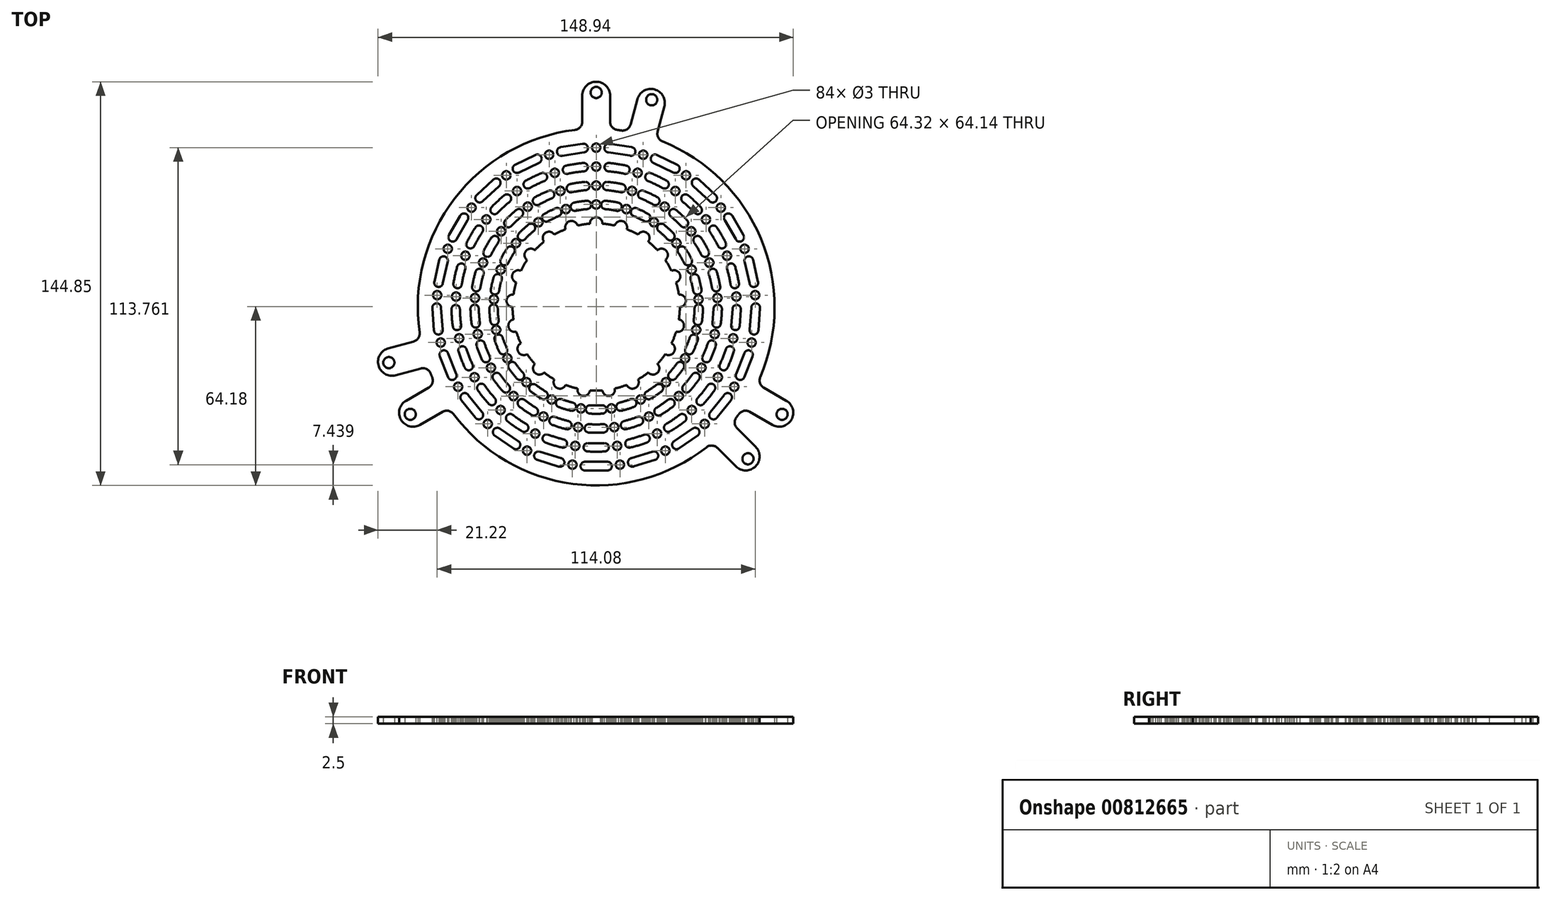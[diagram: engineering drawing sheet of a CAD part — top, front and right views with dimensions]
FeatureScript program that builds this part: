
annotation { "Feature Type Name" : "Feature", "Feature Type Description" : "" }
export const myFeature = defineFeature(function(context is Context, id is Id, definition is map)
    precondition{}
    {
        {
            var Q0;
            Q0=qCreatedBy(makeId("Top.planeOp"),FACE);
            var sketch = newSketch(context, id + "F0", { "sketchPlane" : qUnion([Q0])});
            skCircle(sketch, "E0", {"center": v(0, 0) * mm, "radius": 30 * mm});
            skCircle(sketch, "E1", {"center": v(0, 0) * mm, "radius": 64 * mm});
            skCircle(sketch, "E2", {"center": v(0, 0) * mm, "radius": 77 * mm, "construction": true});
            skCircle(sketch, "E3", {"center": v(0, 0) * mm, "radius": 81 * mm, "construction": true});
            skLineSegment(sketch, "E4", {"start": v(0, 0) * mm, "end": v(0, 81) * mm, "construction": true});
            skLineSegment(sketch, "E5", {"start": v(20.96, 78.24) * mm, "end": v(0, 0) * mm, "construction": true});
            skLineSegment(sketch, "E6", {"start": v(-5, 63.8) * mm, "end": v(-5, 80.85) * mm});
            skLineSegment(sketch, "E7", {"start": v(-5, 80.85) * mm, "end": v(5, 80.85) * mm});
            skLineSegment(sketch, "E8", {"start": v(5, 80.85) * mm, "end": v(5, 63.8) * mm});
            skCircle(sketch, "E9", {"center": v(0, 36.8) * mm, "radius": 1.5 * mm});
            skCircle(sketch, "E10", {"center": v(0, 43.6) * mm, "radius": 1.5 * mm});
            skCircle(sketch, "E11", {"center": v(0, 50.4) * mm, "radius": 1.5 * mm});
            skCircle(sketch, "E12", {"center": v(0, 57.2) * mm, "radius": 1.5 * mm});
            skCircle(sketch, "E13.1.0", {"center": v(-10.85, 35.17) * mm, "radius": 1.5 * mm});
            skCircle(sketch, "E13.1.1", {"center": v(-12.85, 41.66) * mm, "radius": 1.5 * mm});
            skCircle(sketch, "E13.1.2", {"center": v(-14.86, 48.16) * mm, "radius": 1.5 * mm});
            skCircle(sketch, "E13.1.3", {"center": v(-16.86, 54.66) * mm, "radius": 1.5 * mm});
            skCircle(sketch, "E13.2.0", {"center": v(-20.73, 30.4) * mm, "radius": 1.5 * mm});
            skCircle(sketch, "E13.2.1", {"center": v(-24.56, 36.02) * mm, "radius": 1.5 * mm});
            skCircle(sketch, "E13.2.2", {"center": v(-28.4, 41.64) * mm, "radius": 1.5 * mm});
            skCircle(sketch, "E13.2.3", {"center": v(-32.22, 47.26) * mm, "radius": 1.5 * mm});
            skCircle(sketch, "E14.1.3.0", {"center": v(-28.77, 22.94) * mm, "radius": 1.5 * mm});
            skCircle(sketch, "E14.2.3.0", {"center": v(-34.09, 27.18) * mm, "radius": 1.5 * mm});
            skCircle(sketch, "E14.4.3.0", {"center": v(-39.4, 31.42) * mm, "radius": 1.5 * mm});
            skCircle(sketch, "E14.6.3.0", {"center": v(-44.72, 35.66) * mm, "radius": 1.5 * mm});
            skCircle(sketch, "E14.1.4.0", {"center": v(-34.26, 13.44) * mm, "radius": 1.5 * mm});
            skCircle(sketch, "E14.2.4.0", {"center": v(-40.59, 15.93) * mm, "radius": 1.5 * mm});
            skCircle(sketch, "E14.4.4.0", {"center": v(-46.92, 18.41) * mm, "radius": 1.5 * mm});
            skCircle(sketch, "E14.6.4.0", {"center": v(-53.25, 20.9) * mm, "radius": 1.5 * mm});
            skCircle(sketch, "E14.1.5.0", {"center": v(-36.7, 2.75) * mm, "radius": 1.5 * mm});
            skCircle(sketch, "E14.2.5.0", {"center": v(-43.48, 3.26) * mm, "radius": 1.5 * mm});
            skCircle(sketch, "E14.4.5.0", {"center": v(-50.26, 3.77) * mm, "radius": 1.5 * mm});
            skCircle(sketch, "E14.6.5.0", {"center": v(-57.04, 4.27) * mm, "radius": 1.5 * mm});
            skCircle(sketch, "E14.1.6.0", {"center": v(-35.88, -8.19) * mm, "radius": 1.5 * mm});
            skCircle(sketch, "E14.2.6.0", {"center": v(-42.5, -9.7) * mm, "radius": 1.5 * mm});
            skCircle(sketch, "E14.4.6.0", {"center": v(-49.14, -11.22) * mm, "radius": 1.5 * mm});
            skCircle(sketch, "E14.6.6.0", {"center": v(-55.77, -12.73) * mm, "radius": 1.5 * mm});
            skCircle(sketch, "E14.1.7.0", {"center": v(-31.87, -18.4) * mm, "radius": 1.5 * mm});
            skCircle(sketch, "E14.2.7.0", {"center": v(-37.76, -21.8) * mm, "radius": 1.5 * mm});
            skCircle(sketch, "E14.4.7.0", {"center": v(-43.65, -25.2) * mm, "radius": 1.5 * mm});
            skCircle(sketch, "E14.6.7.0", {"center": v(-49.54, -28.6) * mm, "radius": 1.5 * mm});
            skCircle(sketch, "E14.1.8.0", {"center": v(-25.03, -26.98) * mm, "radius": 1.5 * mm});
            skCircle(sketch, "E14.2.8.0", {"center": v(-29.66, -31.96) * mm, "radius": 1.5 * mm});
            skCircle(sketch, "E14.4.8.0", {"center": v(-34.28, -36.95) * mm, "radius": 1.5 * mm});
            skCircle(sketch, "E14.6.8.0", {"center": v(-38.9, -41.93) * mm, "radius": 1.5 * mm});
            skCircle(sketch, "E14.1.9.0", {"center": v(-15.97, -33.16) * mm, "radius": 1.5 * mm});
            skCircle(sketch, "E14.2.9.0", {"center": v(-18.92, -39.28) * mm, "radius": 1.5 * mm});
            skCircle(sketch, "E14.4.9.0", {"center": v(-21.87, -45.4) * mm, "radius": 1.5 * mm});
            skCircle(sketch, "E14.6.9.0", {"center": v(-24.82, -51.54) * mm, "radius": 1.5 * mm});
            skCircle(sketch, "E14.1.10.0", {"center": v(-5.48, -36.39) * mm, "radius": 1.5 * mm});
            skCircle(sketch, "E14.2.10.0", {"center": v(-6.5, -43.11) * mm, "radius": 1.5 * mm});
            skCircle(sketch, "E14.4.10.0", {"center": v(-7.51, -49.84) * mm, "radius": 1.5 * mm});
            skCircle(sketch, "E14.6.10.0", {"center": v(-8.53, -56.56) * mm, "radius": 1.5 * mm});
            skCircle(sketch, "E14.1.11.0", {"center": v(5.48, -36.39) * mm, "radius": 1.5 * mm});
            skCircle(sketch, "E14.2.11.0", {"center": v(6.5, -43.11) * mm, "radius": 1.5 * mm});
            skCircle(sketch, "E14.4.11.0", {"center": v(7.51, -49.84) * mm, "radius": 1.5 * mm});
            skCircle(sketch, "E14.6.11.0", {"center": v(8.53, -56.56) * mm, "radius": 1.5 * mm});
            skCircle(sketch, "E14.1.12.0", {"center": v(15.97, -33.16) * mm, "radius": 1.5 * mm});
            skCircle(sketch, "E14.2.12.0", {"center": v(18.92, -39.28) * mm, "radius": 1.5 * mm});
            skCircle(sketch, "E14.4.12.0", {"center": v(21.87, -45.4) * mm, "radius": 1.5 * mm});
            skCircle(sketch, "E14.6.12.0", {"center": v(24.82, -51.54) * mm, "radius": 1.5 * mm});
            skCircle(sketch, "E14.1.13.0", {"center": v(25.03, -26.98) * mm, "radius": 1.5 * mm});
            skCircle(sketch, "E14.2.13.0", {"center": v(29.66, -31.96) * mm, "radius": 1.5 * mm});
            skCircle(sketch, "E14.4.13.0", {"center": v(34.28, -36.95) * mm, "radius": 1.5 * mm});
            skCircle(sketch, "E14.6.13.0", {"center": v(38.9, -41.93) * mm, "radius": 1.5 * mm});
            skCircle(sketch, "E14.1.14.0", {"center": v(31.87, -18.4) * mm, "radius": 1.5 * mm});
            skCircle(sketch, "E14.2.14.0", {"center": v(37.76, -21.8) * mm, "radius": 1.5 * mm});
            skCircle(sketch, "E14.4.14.0", {"center": v(43.65, -25.2) * mm, "radius": 1.5 * mm});
            skCircle(sketch, "E14.6.14.0", {"center": v(49.54, -28.6) * mm, "radius": 1.5 * mm});
            skCircle(sketch, "E14.1.15.0", {"center": v(35.88, -8.19) * mm, "radius": 1.5 * mm});
            skCircle(sketch, "E14.2.15.0", {"center": v(42.5, -9.7) * mm, "radius": 1.5 * mm});
            skCircle(sketch, "E14.4.15.0", {"center": v(49.14, -11.22) * mm, "radius": 1.5 * mm});
            skCircle(sketch, "E14.6.15.0", {"center": v(55.77, -12.73) * mm, "radius": 1.5 * mm});
            skCircle(sketch, "E14.1.16.0", {"center": v(36.7, 2.75) * mm, "radius": 1.5 * mm});
            skCircle(sketch, "E14.2.16.0", {"center": v(43.48, 3.26) * mm, "radius": 1.5 * mm});
            skCircle(sketch, "E14.4.16.0", {"center": v(50.26, 3.77) * mm, "radius": 1.5 * mm});
            skCircle(sketch, "E14.6.16.0", {"center": v(57.04, 4.27) * mm, "radius": 1.5 * mm});
            skCircle(sketch, "E14.1.17.0", {"center": v(34.26, 13.44) * mm, "radius": 1.5 * mm});
            skCircle(sketch, "E14.2.17.0", {"center": v(40.59, 15.93) * mm, "radius": 1.5 * mm});
            skCircle(sketch, "E14.4.17.0", {"center": v(46.92, 18.41) * mm, "radius": 1.5 * mm});
            skCircle(sketch, "E14.6.17.0", {"center": v(53.25, 20.9) * mm, "radius": 1.5 * mm});
            skCircle(sketch, "E14.1.18.0", {"center": v(28.77, 22.94) * mm, "radius": 1.5 * mm});
            skCircle(sketch, "E14.2.18.0", {"center": v(34.09, 27.18) * mm, "radius": 1.5 * mm});
            skCircle(sketch, "E14.4.18.0", {"center": v(39.4, 31.42) * mm, "radius": 1.5 * mm});
            skCircle(sketch, "E14.6.18.0", {"center": v(44.72, 35.66) * mm, "radius": 1.5 * mm});
            skCircle(sketch, "E14.1.19.0", {"center": v(20.73, 30.4) * mm, "radius": 1.5 * mm});
            skCircle(sketch, "E14.2.19.0", {"center": v(24.56, 36.02) * mm, "radius": 1.5 * mm});
            skCircle(sketch, "E14.4.19.0", {"center": v(28.4, 41.64) * mm, "radius": 1.5 * mm});
            skCircle(sketch, "E14.6.19.0", {"center": v(32.22, 47.26) * mm, "radius": 1.5 * mm});
            skCircle(sketch, "E14.1.20.0", {"center": v(10.85, 35.17) * mm, "radius": 1.5 * mm});
            skCircle(sketch, "E14.2.20.0", {"center": v(12.85, 41.66) * mm, "radius": 1.5 * mm});
            skCircle(sketch, "E14.4.20.0", {"center": v(14.86, 48.16) * mm, "radius": 1.5 * mm});
            skCircle(sketch, "E14.6.20.0", {"center": v(16.86, 54.66) * mm, "radius": 1.5 * mm});
            skLineSegment(sketch, "E15", {"start": v(0, 0) * mm, "end": v(10.57, 80.3) * mm, "construction": true});
            skLineSegment(sketch, "E16", {"start": v(21.34, 60.34) * mm, "end": v(25.75, 76.8) * mm});
            skLineSegment(sketch, "E17", {"start": v(25.75, 76.8) * mm, "end": v(16.1, 79.38) * mm});
            skLineSegment(sketch, "E18", {"start": v(16.1, 79.38) * mm, "end": v(11.68, 62.92) * mm});
            skCircle(sketch, "E19", {"center": v(0, 77) * mm, "radius": 2 * mm});
            skCircle(sketch, "E20", {"center": v(19.93, 74.38) * mm, "radius": 2 * mm});
            skLineSegment(sketch, "E21.1.0", {"start": v(-52.76, -36.23) * mm, "end": v(-67.51, -44.75) * mm});
            skLineSegment(sketch, "E21.1.1", {"start": v(-67.51, -44.75) * mm, "end": v(-72.51, -36.1) * mm});
            skLineSegment(sketch, "E21.1.2", {"start": v(-72.51, -36.1) * mm, "end": v(-57.76, -27.57) * mm});
            skCircle(sketch, "E21.1.3", {"center": v(-66.68, -38.5) * mm, "radius": 2 * mm});
            skLineSegment(sketch, "E21.1.4", {"start": v(-76.8, -25.75) * mm, "end": v(-60.34, -21.34) * mm});
            skLineSegment(sketch, "E21.1.5", {"start": v(-79.38, -16.1) * mm, "end": v(-76.8, -25.75) * mm});
            skLineSegment(sketch, "E21.1.6", {"start": v(-62.92, -11.68) * mm, "end": v(-79.38, -16.1) * mm});
            skCircle(sketch, "E21.1.7", {"center": v(-74.38, -19.93) * mm, "radius": 2 * mm});
            skLineSegment(sketch, "E21.2.0", {"start": v(57.76, -27.57) * mm, "end": v(72.51, -36.1) * mm});
            skLineSegment(sketch, "E21.2.1", {"start": v(72.51, -36.1) * mm, "end": v(67.51, -44.75) * mm});
            skLineSegment(sketch, "E21.2.2", {"start": v(67.51, -44.75) * mm, "end": v(52.76, -36.23) * mm});
            skCircle(sketch, "E21.2.3", {"center": v(66.68, -38.5) * mm, "radius": 2 * mm});
            skLineSegment(sketch, "E21.2.4", {"start": v(60.7, -53.63) * mm, "end": v(48.65, -41.58) * mm});
            skLineSegment(sketch, "E21.2.5", {"start": v(53.63, -60.7) * mm, "end": v(60.7, -53.63) * mm});
            skLineSegment(sketch, "E21.2.6", {"start": v(41.58, -48.65) * mm, "end": v(53.63, -60.7) * mm});
            skCircle(sketch, "E21.2.7", {"center": v(54.45, -54.45) * mm, "radius": 2 * mm});
            skSolve(sketch);
        }
        {
            var Q0;
            Q0=makeQuery(id+"F0.imprint","IMPRINT",FACE,{"disambiguationData":[TD([[makeQuery(id+"F0.imprint","IMPRINT",EDGE,{"derivedFrom":sQuery(id+"F0.wireOp",EDGE,"E0")}),-1.0]])]});
            var Q1;
            {var subQ1=sQuery(id+"F0.wireOp",EDGE,"E6");Q1=makeQuery(id+"F0.imprint","IMPRINT",FACE,{"disambiguationData":[TD([[makeQuery(id+"F0.imprint","IMPRINT",EDGE,{"derivedFrom":subQ1}),-1.0]])]});}
            var Q2;
            {var subQ1=sQuery(id+"F0.wireOp",EDGE,"E16");Q2=makeQuery(id+"F0.imprint","IMPRINT",FACE,{"disambiguationData":[TD([[makeQuery(id+"F0.imprint","IMPRINT",EDGE,{"derivedFrom":subQ1}),1.0]])]});}
            var Q3;
            {var subQ1=sQuery(id+"F0.wireOp",EDGE,"E21.2.0");Q3=makeQuery(id+"F0.imprint","IMPRINT",FACE,{"disambiguationData":[TD([[makeQuery(id+"F0.imprint","IMPRINT",EDGE,{"derivedFrom":subQ1}),-1.0]])]});}
            var Q4;
            {var subQ0=sQuery(id+"F0.wireOp",EDGE,"E21.2.4");Q4=makeQuery(id+"F0.imprint","IMPRINT",FACE,{"disambiguationData":[TD([[makeQuery(id+"F0.imprint","IMPRINT",EDGE,{"derivedFrom":subQ0}),1.0]])]});}
            var Q5;
            {var subQ0=sQuery(id+"F0.wireOp",EDGE,"E21.1.0");Q5=makeQuery(id+"F0.imprint","IMPRINT",FACE,{"disambiguationData":[TD([[makeQuery(id+"F0.imprint","IMPRINT",EDGE,{"derivedFrom":subQ0}),-1.0]])]});}
            var Q6;
            {var subQ1=sQuery(id+"F0.wireOp",EDGE,"E21.1.4");Q6=makeQuery(id+"F0.imprint","IMPRINT",FACE,{"disambiguationData":[TD([[makeQuery(id+"F0.imprint","IMPRINT",EDGE,{"derivedFrom":subQ1}),1.0]])]});}
            extrude(context, id + "F1", {"entities" : qUnion([Q0, Q1, Q2, Q3, Q4, Q5, Q6]), "depth" : 2.5 * mm, "offsetDistance" : 25 * mm});
        }
        {
            var Q0;
            Q0=makeQuery(id+"F1.opExtrude","SWEPT_EDGE",EDGE,{"disambiguationData":[OSD([sQuery(id+"F0.wireOp",EDGE,"E6"),sQuery(id+"F0.wireOp",EDGE,"E7")])]});
            var Q1;
            Q1=makeQuery(id+"F1.opExtrude","SWEPT_EDGE",EDGE,{"disambiguationData":[OSD([sQuery(id+"F0.wireOp",EDGE,"E7"),sQuery(id+"F0.wireOp",EDGE,"E8")])]});
            var Q2;
            Q2=makeQuery(id+"F1.opExtrude","SWEPT_EDGE",EDGE,{"disambiguationData":[OSD([sQuery(id+"F0.wireOp",EDGE,"E17"),sQuery(id+"F0.wireOp",EDGE,"E18")])]});
            var Q3;
            Q3=makeQuery(id+"F1.opExtrude","SWEPT_EDGE",EDGE,{"disambiguationData":[OSD([sQuery(id+"F0.wireOp",EDGE,"E16"),sQuery(id+"F0.wireOp",EDGE,"E17")])]});
            var Q4;
            Q4=makeQuery(id+"F1.opExtrude","SWEPT_EDGE",EDGE,{"disambiguationData":[OSD([sQuery(id+"F0.wireOp",EDGE,"E21.1.0"),sQuery(id+"F0.wireOp",EDGE,"E21.1.1")])]});
            var Q5;
            Q5=makeQuery(id+"F1.opExtrude","SWEPT_EDGE",EDGE,{"disambiguationData":[OSD([sQuery(id+"F0.wireOp",EDGE,"E21.1.1"),sQuery(id+"F0.wireOp",EDGE,"E21.1.2")])]});
            var Q6;
            Q6=makeQuery(id+"F1.opExtrude","SWEPT_EDGE",EDGE,{"disambiguationData":[OSD([sQuery(id+"F0.wireOp",EDGE,"E21.1.4"),sQuery(id+"F0.wireOp",EDGE,"E21.1.5")])]});
            var Q7;
            Q7=makeQuery(id+"F1.opExtrude","SWEPT_EDGE",EDGE,{"disambiguationData":[OSD([sQuery(id+"F0.wireOp",EDGE,"E21.1.5"),sQuery(id+"F0.wireOp",EDGE,"E21.1.6")])]});
            var Q8;
            Q8=makeQuery(id+"F1.opExtrude","SWEPT_EDGE",EDGE,{"disambiguationData":[OSD([sQuery(id+"F0.wireOp",EDGE,"E21.2.4"),sQuery(id+"F0.wireOp",EDGE,"E21.2.5")])]});
            var Q9;
            Q9=makeQuery(id+"F1.opExtrude","SWEPT_EDGE",EDGE,{"disambiguationData":[OSD([sQuery(id+"F0.wireOp",EDGE,"E21.2.5"),sQuery(id+"F0.wireOp",EDGE,"E21.2.6")])]});
            var Q10;
            Q10=makeQuery(id+"F1.opExtrude","SWEPT_EDGE",EDGE,{"disambiguationData":[OSD([sQuery(id+"F0.wireOp",EDGE,"E21.2.1"),sQuery(id+"F0.wireOp",EDGE,"E21.2.2")])]});
            var Q11;
            Q11=makeQuery(id+"F1.opExtrude","SWEPT_EDGE",EDGE,{"disambiguationData":[OSD([sQuery(id+"F0.wireOp",EDGE,"E21.2.0"),sQuery(id+"F0.wireOp",EDGE,"E21.2.1")])]});
            fillet(context, id + "F2", {"entities" : qUnion([Q0, Q1, Q2, Q3, Q4, Q5, Q6, Q7, Q8, Q9, Q10, Q11]), "radius" : 5 * mm, "tangentPropagation" : true, "allowEdgeOverflow" : false});
        }
        {
            var Q0;
            Q0=makeQuery(id+"F1.opExtrude","SWEPT_EDGE",EDGE,{"disambiguationData":[OSD([sQuery(id+"F0.wireOp",EDGE,"E1"),sQuery(id+"F0.wireOp",EDGE,"E8")])]});
            var Q1;
            Q1=makeQuery(id+"F1.opExtrude","SWEPT_EDGE",EDGE,{"disambiguationData":[OSD([sQuery(id+"F0.wireOp",EDGE,"E1"),sQuery(id+"F0.wireOp",EDGE,"E6")])]});
            var Q2;
            Q2=makeQuery(id+"F1.opExtrude","SWEPT_EDGE",EDGE,{"disambiguationData":[OSD([sQuery(id+"F0.wireOp",EDGE,"E1"),sQuery(id+"F0.wireOp",EDGE,"E21.1.2")])]});
            var Q3;
            Q3=makeQuery(id+"F1.opExtrude","SWEPT_EDGE",EDGE,{"disambiguationData":[OSD([sQuery(id+"F0.wireOp",EDGE,"E1"),sQuery(id+"F0.wireOp",EDGE,"E21.1.6")])]});
            var Q4;
            Q4=makeQuery(id+"F1.opExtrude","SWEPT_EDGE",EDGE,{"disambiguationData":[OSD([sQuery(id+"F0.wireOp",EDGE,"E1"),sQuery(id+"F0.wireOp",EDGE,"E21.1.0")])]});
            var Q5;
            Q5=makeQuery(id+"F1.opExtrude","SWEPT_EDGE",EDGE,{"disambiguationData":[OSD([sQuery(id+"F0.wireOp",EDGE,"E1"),sQuery(id+"F0.wireOp",EDGE,"E21.1.4")])]});
            var Q6;
            Q6=makeQuery(id+"F1.opExtrude","SWEPT_EDGE",EDGE,{"disambiguationData":[OSD([sQuery(id+"F0.wireOp",EDGE,"E1"),sQuery(id+"F0.wireOp",EDGE,"E16")])]});
            var Q7;
            Q7=makeQuery(id+"F1.opExtrude","SWEPT_EDGE",EDGE,{"disambiguationData":[OSD([sQuery(id+"F0.wireOp",EDGE,"E1"),sQuery(id+"F0.wireOp",EDGE,"E18")])]});
            var Q8;
            Q8=makeQuery(id+"F1.opExtrude","SWEPT_EDGE",EDGE,{"disambiguationData":[OSD([sQuery(id+"F0.wireOp",EDGE,"E1"),sQuery(id+"F0.wireOp",EDGE,"E21.2.0")])]});
            var Q9;
            Q9=makeQuery(id+"F1.opExtrude","SWEPT_EDGE",EDGE,{"disambiguationData":[OSD([sQuery(id+"F0.wireOp",EDGE,"E1"),sQuery(id+"F0.wireOp",EDGE,"E21.2.4")])]});
            var Q10;
            Q10=makeQuery(id+"F1.opExtrude","SWEPT_EDGE",EDGE,{"disambiguationData":[OSD([sQuery(id+"F0.wireOp",EDGE,"E1"),sQuery(id+"F0.wireOp",EDGE,"E21.2.2")])]});
            var Q11;
            Q11=makeQuery(id+"F1.opExtrude","SWEPT_EDGE",EDGE,{"disambiguationData":[OSD([sQuery(id+"F0.wireOp",EDGE,"E1"),sQuery(id+"F0.wireOp",EDGE,"E21.2.6")])]});
            fillet(context, id + "F3", {"entities" : qUnion([Q0, Q1, Q2, Q3, Q4, Q5, Q6, Q7, Q8, Q9, Q10, Q11]), "radius" : 3 * mm, "tangentPropagation" : true, "allowEdgeOverflow" : false});
        }
        {
            var Q0;
            Q0=makeQuery(id+"F1.opExtrude","CAP_FACE",FACE,{"disambiguationData":[OSD([sQuery(id+"F0.wireOp",EDGE,"E0"),sQuery(id+"F0.wireOp",EDGE,"E1"),sQuery(id+"F0.wireOp",EDGE,"E6"),sQuery(id+"F0.wireOp",EDGE,"E7"),sQuery(id+"F0.wireOp",EDGE,"E8"),sQuery(id+"F0.wireOp",EDGE,"E9"),sQuery(id+"F0.wireOp",EDGE,"E10"),sQuery(id+"F0.wireOp",EDGE,"E11"),sQuery(id+"F0.wireOp",EDGE,"E12"),sQuery(id+"F0.wireOp",EDGE,"E13.1.0"),sQuery(id+"F0.wireOp",EDGE,"E13.1.1"),sQuery(id+"F0.wireOp",EDGE,"E13.1.2"),sQuery(id+"F0.wireOp",EDGE,"E13.1.3"),sQuery(id+"F0.wireOp",EDGE,"E13.2.0"),sQuery(id+"F0.wireOp",EDGE,"E13.2.1"),sQuery(id+"F0.wireOp",EDGE,"E13.2.2"),sQuery(id+"F0.wireOp",EDGE,"E13.2.3"),sQuery(id+"F0.wireOp",EDGE,"E14.1.3.0"),sQuery(id+"F0.wireOp",EDGE,"E14.2.3.0"),sQuery(id+"F0.wireOp",EDGE,"E14.4.3.0"),sQuery(id+"F0.wireOp",EDGE,"E14.6.3.0"),sQuery(id+"F0.wireOp",EDGE,"E14.1.4.0"),sQuery(id+"F0.wireOp",EDGE,"E14.2.4.0"),sQuery(id+"F0.wireOp",EDGE,"E14.4.4.0"),sQuery(id+"F0.wireOp",EDGE,"E14.6.4.0"),sQuery(id+"F0.wireOp",EDGE,"E14.1.5.0"),sQuery(id+"F0.wireOp",EDGE,"E14.2.5.0"),sQuery(id+"F0.wireOp",EDGE,"E14.4.5.0"),sQuery(id+"F0.wireOp",EDGE,"E14.6.5.0"),sQuery(id+"F0.wireOp",EDGE,"E14.1.6.0"),sQuery(id+"F0.wireOp",EDGE,"E14.2.6.0"),sQuery(id+"F0.wireOp",EDGE,"E14.4.6.0"),sQuery(id+"F0.wireOp",EDGE,"E14.6.6.0"),sQuery(id+"F0.wireOp",EDGE,"E14.1.7.0"),sQuery(id+"F0.wireOp",EDGE,"E14.2.7.0"),sQuery(id+"F0.wireOp",EDGE,"E14.4.7.0"),sQuery(id+"F0.wireOp",EDGE,"E14.6.7.0"),sQuery(id+"F0.wireOp",EDGE,"E14.1.8.0"),sQuery(id+"F0.wireOp",EDGE,"E14.2.8.0"),sQuery(id+"F0.wireOp",EDGE,"E14.4.8.0"),sQuery(id+"F0.wireOp",EDGE,"E14.6.8.0"),sQuery(id+"F0.wireOp",EDGE,"E14.1.9.0"),sQuery(id+"F0.wireOp",EDGE,"E14.2.9.0"),sQuery(id+"F0.wireOp",EDGE,"E14.4.9.0"),sQuery(id+"F0.wireOp",EDGE,"E14.6.9.0"),sQuery(id+"F0.wireOp",EDGE,"E14.1.10.0"),sQuery(id+"F0.wireOp",EDGE,"E14.2.10.0"),sQuery(id+"F0.wireOp",EDGE,"E14.4.10.0"),sQuery(id+"F0.wireOp",EDGE,"E14.6.10.0"),sQuery(id+"F0.wireOp",EDGE,"E14.1.11.0"),sQuery(id+"F0.wireOp",EDGE,"E14.2.11.0"),sQuery(id+"F0.wireOp",EDGE,"E14.4.11.0"),sQuery(id+"F0.wireOp",EDGE,"E14.6.11.0"),sQuery(id+"F0.wireOp",EDGE,"E14.1.12.0"),sQuery(id+"F0.wireOp",EDGE,"E14.2.12.0"),sQuery(id+"F0.wireOp",EDGE,"E14.4.12.0"),sQuery(id+"F0.wireOp",EDGE,"E14.6.12.0"),sQuery(id+"F0.wireOp",EDGE,"E14.1.13.0"),sQuery(id+"F0.wireOp",EDGE,"E14.2.13.0"),sQuery(id+"F0.wireOp",EDGE,"E14.4.13.0"),sQuery(id+"F0.wireOp",EDGE,"E14.6.13.0"),sQuery(id+"F0.wireOp",EDGE,"E14.1.14.0"),sQuery(id+"F0.wireOp",EDGE,"E14.2.14.0"),sQuery(id+"F0.wireOp",EDGE,"E14.4.14.0"),sQuery(id+"F0.wireOp",EDGE,"E14.6.14.0"),sQuery(id+"F0.wireOp",EDGE,"E14.1.15.0"),sQuery(id+"F0.wireOp",EDGE,"E14.2.15.0"),sQuery(id+"F0.wireOp",EDGE,"E14.4.15.0"),sQuery(id+"F0.wireOp",EDGE,"E14.6.15.0"),sQuery(id+"F0.wireOp",EDGE,"E14.1.16.0"),sQuery(id+"F0.wireOp",EDGE,"E14.2.16.0"),sQuery(id+"F0.wireOp",EDGE,"E14.4.16.0"),sQuery(id+"F0.wireOp",EDGE,"E14.6.16.0"),sQuery(id+"F0.wireOp",EDGE,"E14.1.17.0"),sQuery(id+"F0.wireOp",EDGE,"E14.2.17.0"),sQuery(id+"F0.wireOp",EDGE,"E14.4.17.0"),sQuery(id+"F0.wireOp",EDGE,"E14.6.17.0"),sQuery(id+"F0.wireOp",EDGE,"E14.1.18.0"),sQuery(id+"F0.wireOp",EDGE,"E14.2.18.0"),sQuery(id+"F0.wireOp",EDGE,"E14.4.18.0"),sQuery(id+"F0.wireOp",EDGE,"E14.6.18.0"),sQuery(id+"F0.wireOp",EDGE,"E14.1.19.0"),sQuery(id+"F0.wireOp",EDGE,"E14.2.19.0"),sQuery(id+"F0.wireOp",EDGE,"E14.4.19.0"),sQuery(id+"F0.wireOp",EDGE,"E14.6.19.0"),sQuery(id+"F0.wireOp",EDGE,"E14.1.20.0"),sQuery(id+"F0.wireOp",EDGE,"E14.2.20.0"),sQuery(id+"F0.wireOp",EDGE,"E14.4.20.0"),sQuery(id+"F0.wireOp",EDGE,"E14.6.20.0"),sQuery(id+"F0.wireOp",EDGE,"E16"),sQuery(id+"F0.wireOp",EDGE,"E17"),sQuery(id+"F0.wireOp",EDGE,"E18"),sQuery(id+"F0.wireOp",EDGE,"E19"),sQuery(id+"F0.wireOp",EDGE,"E20"),sQuery(id+"F0.wireOp",EDGE,"E21.1.0"),sQuery(id+"F0.wireOp",EDGE,"E21.1.1"),sQuery(id+"F0.wireOp",EDGE,"E21.1.2"),sQuery(id+"F0.wireOp",EDGE,"E21.1.3"),sQuery(id+"F0.wireOp",EDGE,"E21.1.4"),sQuery(id+"F0.wireOp",EDGE,"E21.1.5"),sQuery(id+"F0.wireOp",EDGE,"E21.1.6"),sQuery(id+"F0.wireOp",EDGE,"E21.1.7"),sQuery(id+"F0.wireOp",EDGE,"E21.2.0"),sQuery(id+"F0.wireOp",EDGE,"E21.2.1"),sQuery(id+"F0.wireOp",EDGE,"E21.2.2"),sQuery(id+"F0.wireOp",EDGE,"E21.2.3"),sQuery(id+"F0.wireOp",EDGE,"E21.2.4"),sQuery(id+"F0.wireOp",EDGE,"E21.2.5"),sQuery(id+"F0.wireOp",EDGE,"E21.2.6"),sQuery(id+"F0.wireOp",EDGE,"E21.2.7")])],"isStart":false});
            var sketch = newSketch(context, id + "F4", { "sketchPlane" : qUnion([Q0])});
            skCircle(sketch, "E22", {"center": v(0, 0) * mm, "radius": 58.78 * mm, "construction": true});
            skCircle(sketch, "E23", {"center": v(0, 0) * mm, "radius": 55.66 * mm, "construction": true});
            skLineSegment(sketch, "E24", {"start": v(-42.93, 40.15) * mm, "end": v(-40.66, 38.02) * mm});
            skLineSegment(sketch, "E25", {"start": v(-34.9, 43.37) * mm, "end": v(-36.81, 45.82) * mm});
            skLineSegment(sketch, "E26", {"start": v(-40.66, 38.02) * mm, "end": v(-34.9, 43.37) * mm});
            skLineSegment(sketch, "E27", {"start": v(-36.81, 45.82) * mm, "end": v(-42.93, 40.15) * mm});
            skLineSegment(sketch, "E28.1.0", {"start": v(-52.85, 25.72) * mm, "end": v(-50.06, 24.35) * mm});
            skLineSegment(sketch, "E28.1.1", {"start": v(-50.06, 24.35) * mm, "end": v(-46.13, 31.16) * mm});
            skLineSegment(sketch, "E28.1.2", {"start": v(-46.13, 31.16) * mm, "end": v(-48.68, 32.94) * mm});
            skLineSegment(sketch, "E28.1.3", {"start": v(-48.68, 32.94) * mm, "end": v(-52.85, 25.72) * mm});
            skLineSegment(sketch, "E28.2.0", {"start": v(-58.09, 9) * mm, "end": v(-55, 8.51) * mm});
            skLineSegment(sketch, "E28.2.1", {"start": v(-55, 8.51) * mm, "end": v(-53.26, 16.18) * mm});
            skLineSegment(sketch, "E28.2.2", {"start": v(-53.26, 16.18) * mm, "end": v(-56.23, 17.12) * mm});
            skLineSegment(sketch, "E28.2.3", {"start": v(-56.23, 17.12) * mm, "end": v(-58.09, 9) * mm});
            skLineSegment(sketch, "E29.1.3.0", {"start": v(-58.16, -8.53) * mm, "end": v(-55.07, -8.08) * mm});
            skLineSegment(sketch, "E29.3.3.0", {"start": v(-55.07, -8.08) * mm, "end": v(-55.66, -0.24) * mm});
            skLineSegment(sketch, "E29.6.3.0", {"start": v(-55.66, -0.24) * mm, "end": v(-58.78, -0.2) * mm});
            skLineSegment(sketch, "E29.9.3.0", {"start": v(-58.78, -0.2) * mm, "end": v(-58.16, -8.53) * mm});
            skLineSegment(sketch, "E29.1.4.0", {"start": v(-53.06, -25.29) * mm, "end": v(-50.24, -23.96) * mm});
            skLineSegment(sketch, "E29.3.4.0", {"start": v(-50.24, -23.96) * mm, "end": v(-53.12, -16.63) * mm});
            skLineSegment(sketch, "E29.6.4.0", {"start": v(-53.12, -16.63) * mm, "end": v(-56.1, -17.53) * mm});
            skLineSegment(sketch, "E29.9.4.0", {"start": v(-56.1, -17.53) * mm, "end": v(-53.06, -25.29) * mm});
            skLineSegment(sketch, "E29.1.5.0", {"start": v(-43.25, -39.8) * mm, "end": v(-40.95, -37.7) * mm});
            skLineSegment(sketch, "E29.3.5.0", {"start": v(-40.95, -37.7) * mm, "end": v(-45.86, -31.55) * mm});
            skLineSegment(sketch, "E29.6.5.0", {"start": v(-45.86, -31.55) * mm, "end": v(-48.45, -33.28) * mm});
            skLineSegment(sketch, "E29.9.5.0", {"start": v(-48.45, -33.28) * mm, "end": v(-43.25, -39.8) * mm});
            skLineSegment(sketch, "E29.1.6.0", {"start": v(-29.6, -50.79) * mm, "end": v(-28.02, -48.1) * mm});
            skLineSegment(sketch, "E29.3.6.0", {"start": v(-28.02, -48.1) * mm, "end": v(-34.52, -43.67) * mm});
            skLineSegment(sketch, "E29.6.6.0", {"start": v(-34.52, -43.67) * mm, "end": v(-36.48, -46.09) * mm});
            skLineSegment(sketch, "E29.9.6.0", {"start": v(-36.48, -46.09) * mm, "end": v(-29.6, -50.79) * mm});
            skLineSegment(sketch, "E29.1.7.0", {"start": v(-13.31, -57.25) * mm, "end": v(-12.6, -54.22) * mm});
            skLineSegment(sketch, "E29.3.7.0", {"start": v(-12.6, -54.22) * mm, "end": v(-20.11, -51.9) * mm});
            skLineSegment(sketch, "E29.6.7.0", {"start": v(-20.11, -51.9) * mm, "end": v(-21.28, -54.8) * mm});
            skLineSegment(sketch, "E29.9.7.0", {"start": v(-21.28, -54.8) * mm, "end": v(-13.31, -57.25) * mm});
            skLineSegment(sketch, "E29.1.8.0", {"start": v(4.16, -58.63) * mm, "end": v(3.94, -55.52) * mm});
            skLineSegment(sketch, "E29.3.8.0", {"start": v(3.94, -55.52) * mm, "end": v(-3.92, -55.53) * mm});
            skLineSegment(sketch, "E29.6.8.0", {"start": v(-3.92, -55.53) * mm, "end": v(-4.18, -58.63) * mm});
            skLineSegment(sketch, "E29.9.8.0", {"start": v(-4.18, -58.63) * mm, "end": v(4.16, -58.63) * mm});
            skLineSegment(sketch, "E29.1.9.0", {"start": v(21.25, -54.8) * mm, "end": v(20.13, -51.9) * mm});
            skLineSegment(sketch, "E29.3.9.0", {"start": v(20.13, -51.9) * mm, "end": v(12.62, -54.21) * mm});
            skLineSegment(sketch, "E29.6.9.0", {"start": v(12.62, -54.21) * mm, "end": v(13.28, -57.26) * mm});
            skLineSegment(sketch, "E29.9.9.0", {"start": v(13.28, -57.26) * mm, "end": v(21.25, -54.8) * mm});
            skLineSegment(sketch, "E29.1.10.0", {"start": v(36.46, -46.1) * mm, "end": v(34.54, -43.65) * mm});
            skLineSegment(sketch, "E29.3.10.0", {"start": v(34.54, -43.65) * mm, "end": v(28.04, -48.09) * mm});
            skLineSegment(sketch, "E29.6.10.0", {"start": v(28.04, -48.09) * mm, "end": v(29.57, -50.8) * mm});
            skLineSegment(sketch, "E29.9.10.0", {"start": v(29.57, -50.8) * mm, "end": v(36.46, -46.1) * mm});
            skLineSegment(sketch, "E29.1.11.0", {"start": v(48.43, -33.3) * mm, "end": v(45.87, -31.53) * mm});
            skLineSegment(sketch, "E29.3.11.0", {"start": v(45.87, -31.53) * mm, "end": v(40.97, -37.69) * mm});
            skLineSegment(sketch, "E29.6.11.0", {"start": v(40.97, -37.69) * mm, "end": v(43.23, -39.83) * mm});
            skLineSegment(sketch, "E29.9.11.0", {"start": v(43.23, -39.83) * mm, "end": v(48.43, -33.3) * mm});
            skLineSegment(sketch, "E29.1.12.0", {"start": v(56.1, -17.55) * mm, "end": v(53.13, -16.61) * mm});
            skLineSegment(sketch, "E29.3.12.0", {"start": v(53.13, -16.61) * mm, "end": v(50.25, -23.94) * mm});
            skLineSegment(sketch, "E29.6.12.0", {"start": v(50.25, -23.94) * mm, "end": v(53.05, -25.31) * mm});
            skLineSegment(sketch, "E29.9.12.0", {"start": v(53.05, -25.31) * mm, "end": v(56.1, -17.55) * mm});
            skLineSegment(sketch, "E29.1.13.0", {"start": v(58.78, -0.24) * mm, "end": v(55.66, -0.22) * mm});
            skLineSegment(sketch, "E29.3.13.0", {"start": v(55.66, -0.22) * mm, "end": v(55.08, -8.06) * mm});
            skLineSegment(sketch, "E29.6.13.0", {"start": v(55.08, -8.06) * mm, "end": v(58.15, -8.55) * mm});
            skLineSegment(sketch, "E29.9.13.0", {"start": v(58.15, -8.55) * mm, "end": v(58.78, -0.24) * mm});
            skLineSegment(sketch, "E29.1.14.0", {"start": v(56.24, 17.1) * mm, "end": v(53.25, 16.2) * mm});
            skLineSegment(sketch, "E29.3.14.0", {"start": v(53.25, 16.2) * mm, "end": v(55, 8.53) * mm});
            skLineSegment(sketch, "E29.6.14.0", {"start": v(55, 8.53) * mm, "end": v(58.1, 8.97) * mm});
            skLineSegment(sketch, "E29.9.14.0", {"start": v(58.1, 8.97) * mm, "end": v(56.24, 17.1) * mm});
            skLineSegment(sketch, "E29.1.15.0", {"start": v(48.7, 32.92) * mm, "end": v(46.11, 31.18) * mm});
            skLineSegment(sketch, "E29.3.15.0", {"start": v(46.11, 31.18) * mm, "end": v(50.05, 24.37) * mm});
            skLineSegment(sketch, "E29.6.15.0", {"start": v(50.05, 24.37) * mm, "end": v(52.87, 25.7) * mm});
            skLineSegment(sketch, "E29.9.15.0", {"start": v(52.87, 25.7) * mm, "end": v(48.7, 32.92) * mm});
            skLineSegment(sketch, "E29.1.16.0", {"start": v(36.83, 45.8) * mm, "end": v(34.87, 43.38) * mm});
            skLineSegment(sketch, "E29.3.16.0", {"start": v(34.87, 43.38) * mm, "end": v(40.64, 38.04) * mm});
            skLineSegment(sketch, "E29.6.16.0", {"start": v(40.64, 38.04) * mm, "end": v(42.95, 40.13) * mm});
            skLineSegment(sketch, "E29.9.16.0", {"start": v(42.95, 40.13) * mm, "end": v(36.83, 45.8) * mm});
            skLineSegment(sketch, "E29.1.17.0", {"start": v(21.7, 54.63) * mm, "end": v(20.54, 51.74) * mm});
            skLineSegment(sketch, "E29.3.17.0", {"start": v(20.54, 51.74) * mm, "end": v(27.63, 48.32) * mm});
            skLineSegment(sketch, "E29.6.17.0", {"start": v(27.63, 48.32) * mm, "end": v(29.2, 51) * mm});
            skLineSegment(sketch, "E29.9.17.0", {"start": v(29.2, 51) * mm, "end": v(21.7, 54.63) * mm});
            skLineSegment(sketch, "E29.1.18.0", {"start": v(4.63, 58.6) * mm, "end": v(4.38, 55.5) * mm});
            skLineSegment(sketch, "E29.3.18.0", {"start": v(4.38, 55.5) * mm, "end": v(12.15, 54.32) * mm});
            skLineSegment(sketch, "E29.6.18.0", {"start": v(12.15, 54.32) * mm, "end": v(12.87, 57.35) * mm});
            skLineSegment(sketch, "E29.9.18.0", {"start": v(12.87, 57.35) * mm, "end": v(4.63, 58.6) * mm});
            skLineSegment(sketch, "E29.1.19.0", {"start": v(-12.85, 57.36) * mm, "end": v(-12.18, 54.32) * mm});
            skLineSegment(sketch, "E29.3.19.0", {"start": v(-12.18, 54.32) * mm, "end": v(-4.4, 55.49) * mm});
            skLineSegment(sketch, "E29.6.19.0", {"start": v(-4.4, 55.49) * mm, "end": v(-4.6, 58.6) * mm});
            skLineSegment(sketch, "E29.9.19.0", {"start": v(-4.6, 58.6) * mm, "end": v(-12.85, 57.36) * mm});
            skLineSegment(sketch, "E29.1.20.0", {"start": v(-29.18, 51.02) * mm, "end": v(-27.64, 48.31) * mm});
            skLineSegment(sketch, "E29.3.20.0", {"start": v(-27.64, 48.31) * mm, "end": v(-20.56, 51.73) * mm});
            skLineSegment(sketch, "E29.6.20.0", {"start": v(-20.56, 51.73) * mm, "end": v(-21.67, 54.64) * mm});
            skLineSegment(sketch, "E29.9.20.0", {"start": v(-21.67, 54.64) * mm, "end": v(-29.18, 51.02) * mm});
            skSolve(sketch);
        }
        {
            var Q0;
            Q0 = qSketchRegion(id + "F4", true);
            extrude(context, id + "F5", {"entities" : qUnion([Q0]), "operationType" : NewBodyOperationType.REMOVE, "oppositeDirection" : true, "depth" : 25 * mm, "offsetDistance" : 25 * mm});
        }
        {
            var Q0;
            Q0=makeQuery(id+"F1.opExtrude","CAP_FACE",FACE,{"disambiguationData":[OSD([sQuery(id+"F0.wireOp",EDGE,"E0"),sQuery(id+"F0.wireOp",EDGE,"E1"),sQuery(id+"F0.wireOp",EDGE,"E6"),sQuery(id+"F0.wireOp",EDGE,"E7"),sQuery(id+"F0.wireOp",EDGE,"E8"),sQuery(id+"F0.wireOp",EDGE,"E9"),sQuery(id+"F0.wireOp",EDGE,"E10"),sQuery(id+"F0.wireOp",EDGE,"E11"),sQuery(id+"F0.wireOp",EDGE,"E12"),sQuery(id+"F0.wireOp",EDGE,"E13.1.0"),sQuery(id+"F0.wireOp",EDGE,"E13.1.1"),sQuery(id+"F0.wireOp",EDGE,"E13.1.2"),sQuery(id+"F0.wireOp",EDGE,"E13.1.3"),sQuery(id+"F0.wireOp",EDGE,"E13.2.0"),sQuery(id+"F0.wireOp",EDGE,"E13.2.1"),sQuery(id+"F0.wireOp",EDGE,"E13.2.2"),sQuery(id+"F0.wireOp",EDGE,"E13.2.3"),sQuery(id+"F0.wireOp",EDGE,"E14.1.3.0"),sQuery(id+"F0.wireOp",EDGE,"E14.2.3.0"),sQuery(id+"F0.wireOp",EDGE,"E14.4.3.0"),sQuery(id+"F0.wireOp",EDGE,"E14.6.3.0"),sQuery(id+"F0.wireOp",EDGE,"E14.1.4.0"),sQuery(id+"F0.wireOp",EDGE,"E14.2.4.0"),sQuery(id+"F0.wireOp",EDGE,"E14.4.4.0"),sQuery(id+"F0.wireOp",EDGE,"E14.6.4.0"),sQuery(id+"F0.wireOp",EDGE,"E14.1.5.0"),sQuery(id+"F0.wireOp",EDGE,"E14.2.5.0"),sQuery(id+"F0.wireOp",EDGE,"E14.4.5.0"),sQuery(id+"F0.wireOp",EDGE,"E14.6.5.0"),sQuery(id+"F0.wireOp",EDGE,"E14.1.6.0"),sQuery(id+"F0.wireOp",EDGE,"E14.2.6.0"),sQuery(id+"F0.wireOp",EDGE,"E14.4.6.0"),sQuery(id+"F0.wireOp",EDGE,"E14.6.6.0"),sQuery(id+"F0.wireOp",EDGE,"E14.1.7.0"),sQuery(id+"F0.wireOp",EDGE,"E14.2.7.0"),sQuery(id+"F0.wireOp",EDGE,"E14.4.7.0"),sQuery(id+"F0.wireOp",EDGE,"E14.6.7.0"),sQuery(id+"F0.wireOp",EDGE,"E14.1.8.0"),sQuery(id+"F0.wireOp",EDGE,"E14.2.8.0"),sQuery(id+"F0.wireOp",EDGE,"E14.4.8.0"),sQuery(id+"F0.wireOp",EDGE,"E14.6.8.0"),sQuery(id+"F0.wireOp",EDGE,"E14.1.9.0"),sQuery(id+"F0.wireOp",EDGE,"E14.2.9.0"),sQuery(id+"F0.wireOp",EDGE,"E14.4.9.0"),sQuery(id+"F0.wireOp",EDGE,"E14.6.9.0"),sQuery(id+"F0.wireOp",EDGE,"E14.1.10.0"),sQuery(id+"F0.wireOp",EDGE,"E14.2.10.0"),sQuery(id+"F0.wireOp",EDGE,"E14.4.10.0"),sQuery(id+"F0.wireOp",EDGE,"E14.6.10.0"),sQuery(id+"F0.wireOp",EDGE,"E14.1.11.0"),sQuery(id+"F0.wireOp",EDGE,"E14.2.11.0"),sQuery(id+"F0.wireOp",EDGE,"E14.4.11.0"),sQuery(id+"F0.wireOp",EDGE,"E14.6.11.0"),sQuery(id+"F0.wireOp",EDGE,"E14.1.12.0"),sQuery(id+"F0.wireOp",EDGE,"E14.2.12.0"),sQuery(id+"F0.wireOp",EDGE,"E14.4.12.0"),sQuery(id+"F0.wireOp",EDGE,"E14.6.12.0"),sQuery(id+"F0.wireOp",EDGE,"E14.1.13.0"),sQuery(id+"F0.wireOp",EDGE,"E14.2.13.0"),sQuery(id+"F0.wireOp",EDGE,"E14.4.13.0"),sQuery(id+"F0.wireOp",EDGE,"E14.6.13.0"),sQuery(id+"F0.wireOp",EDGE,"E14.1.14.0"),sQuery(id+"F0.wireOp",EDGE,"E14.2.14.0"),sQuery(id+"F0.wireOp",EDGE,"E14.4.14.0"),sQuery(id+"F0.wireOp",EDGE,"E14.6.14.0"),sQuery(id+"F0.wireOp",EDGE,"E14.1.15.0"),sQuery(id+"F0.wireOp",EDGE,"E14.2.15.0"),sQuery(id+"F0.wireOp",EDGE,"E14.4.15.0"),sQuery(id+"F0.wireOp",EDGE,"E14.6.15.0"),sQuery(id+"F0.wireOp",EDGE,"E14.1.16.0"),sQuery(id+"F0.wireOp",EDGE,"E14.2.16.0"),sQuery(id+"F0.wireOp",EDGE,"E14.4.16.0"),sQuery(id+"F0.wireOp",EDGE,"E14.6.16.0"),sQuery(id+"F0.wireOp",EDGE,"E14.1.17.0"),sQuery(id+"F0.wireOp",EDGE,"E14.2.17.0"),sQuery(id+"F0.wireOp",EDGE,"E14.4.17.0"),sQuery(id+"F0.wireOp",EDGE,"E14.6.17.0"),sQuery(id+"F0.wireOp",EDGE,"E14.1.18.0"),sQuery(id+"F0.wireOp",EDGE,"E14.2.18.0"),sQuery(id+"F0.wireOp",EDGE,"E14.4.18.0"),sQuery(id+"F0.wireOp",EDGE,"E14.6.18.0"),sQuery(id+"F0.wireOp",EDGE,"E14.1.19.0"),sQuery(id+"F0.wireOp",EDGE,"E14.2.19.0"),sQuery(id+"F0.wireOp",EDGE,"E14.4.19.0"),sQuery(id+"F0.wireOp",EDGE,"E14.6.19.0"),sQuery(id+"F0.wireOp",EDGE,"E14.1.20.0"),sQuery(id+"F0.wireOp",EDGE,"E14.2.20.0"),sQuery(id+"F0.wireOp",EDGE,"E14.4.20.0"),sQuery(id+"F0.wireOp",EDGE,"E14.6.20.0"),sQuery(id+"F0.wireOp",EDGE,"E16"),sQuery(id+"F0.wireOp",EDGE,"E17"),sQuery(id+"F0.wireOp",EDGE,"E18"),sQuery(id+"F0.wireOp",EDGE,"E19"),sQuery(id+"F0.wireOp",EDGE,"E20"),sQuery(id+"F0.wireOp",EDGE,"E21.1.0"),sQuery(id+"F0.wireOp",EDGE,"E21.1.1"),sQuery(id+"F0.wireOp",EDGE,"E21.1.2"),sQuery(id+"F0.wireOp",EDGE,"E21.1.3"),sQuery(id+"F0.wireOp",EDGE,"E21.1.4"),sQuery(id+"F0.wireOp",EDGE,"E21.1.5"),sQuery(id+"F0.wireOp",EDGE,"E21.1.6"),sQuery(id+"F0.wireOp",EDGE,"E21.1.7"),sQuery(id+"F0.wireOp",EDGE,"E21.2.0"),sQuery(id+"F0.wireOp",EDGE,"E21.2.1"),sQuery(id+"F0.wireOp",EDGE,"E21.2.2"),sQuery(id+"F0.wireOp",EDGE,"E21.2.3"),sQuery(id+"F0.wireOp",EDGE,"E21.2.4"),sQuery(id+"F0.wireOp",EDGE,"E21.2.5"),sQuery(id+"F0.wireOp",EDGE,"E21.2.6"),sQuery(id+"F0.wireOp",EDGE,"E21.2.7")])],"isStart":false});
            var sketch = newSketch(context, id + "F6", { "sketchPlane" : qUnion([Q0])});
            skCircle(sketch, "E30", {"center": v(-57.22, -0.22) * mm, "radius": 1.56 * mm});
            skCircle(sketch, "E31", {"center": v(-56.62, -8.3) * mm, "radius": 1.56 * mm});
            skCircle(sketch, "E32.1.0", {"center": v(-54.61, -17.08) * mm, "radius": 1.56 * mm});
            skCircle(sketch, "E32.1.1", {"center": v(-51.65, -24.62) * mm, "radius": 1.56 * mm});
            skCircle(sketch, "E32.2.0", {"center": v(-47.15, -32.42) * mm, "radius": 1.56 * mm});
            skCircle(sketch, "E32.2.1", {"center": v(-42.1, -38.75) * mm, "radius": 1.56 * mm});
            skPoint(sketch, "E32.center", {"position": v(0, 0) * mm});
            skCircle(sketch, "E33.1.3.0", {"center": v(-35.5, -44.88) * mm, "radius": 1.56 * mm});
            skCircle(sketch, "E33.2.3.0", {"center": v(-28.8, -49.44) * mm, "radius": 1.56 * mm});
            skCircle(sketch, "E33.1.4.0", {"center": v(-20.7, -53.35) * mm, "radius": 1.56 * mm});
            skCircle(sketch, "E33.2.4.0", {"center": v(-12.95, -55.74) * mm, "radius": 1.56 * mm});
            skCircle(sketch, "E33.1.5.0", {"center": v(-4.05, -57.08) * mm, "radius": 1.56 * mm});
            skCircle(sketch, "E33.2.5.0", {"center": v(4.05, -57.08) * mm, "radius": 1.56 * mm});
            skCircle(sketch, "E33.1.6.0", {"center": v(12.95, -55.74) * mm, "radius": 1.56 * mm});
            skCircle(sketch, "E33.2.6.0", {"center": v(20.7, -53.35) * mm, "radius": 1.56 * mm});
            skCircle(sketch, "E33.1.7.0", {"center": v(28.8, -49.44) * mm, "radius": 1.56 * mm});
            skCircle(sketch, "E33.2.7.0", {"center": v(35.5, -44.88) * mm, "radius": 1.56 * mm});
            skCircle(sketch, "E33.1.8.0", {"center": v(42.1, -38.76) * mm, "radius": 1.56 * mm});
            skCircle(sketch, "E33.2.8.0", {"center": v(47.15, -32.42) * mm, "radius": 1.56 * mm});
            skCircle(sketch, "E33.1.9.0", {"center": v(51.65, -24.63) * mm, "radius": 1.56 * mm});
            skCircle(sketch, "E33.2.9.0", {"center": v(54.61, -17.08) * mm, "radius": 1.56 * mm});
            skCircle(sketch, "E33.1.10.0", {"center": v(56.62, -8.3) * mm, "radius": 1.56 * mm});
            skCircle(sketch, "E33.2.10.0", {"center": v(57.22, -0.23) * mm, "radius": 1.56 * mm});
            skCircle(sketch, "E33.1.11.0", {"center": v(56.55, 8.75) * mm, "radius": 1.56 * mm});
            skCircle(sketch, "E33.2.11.0", {"center": v(54.75, 16.65) * mm, "radius": 1.56 * mm});
            skCircle(sketch, "E33.1.12.0", {"center": v(51.46, 25.03) * mm, "radius": 1.56 * mm});
            skCircle(sketch, "E33.2.12.0", {"center": v(47.4, 32.05) * mm, "radius": 1.56 * mm});
            skCircle(sketch, "E33.1.13.0", {"center": v(41.8, 39.08) * mm, "radius": 1.56 * mm});
            skCircle(sketch, "E33.2.13.0", {"center": v(35.85, 44.6) * mm, "radius": 1.56 * mm});
            skCircle(sketch, "E33.1.14.0", {"center": v(28.42, 49.67) * mm, "radius": 1.56 * mm});
            skCircle(sketch, "E33.2.14.0", {"center": v(21.12, 53.18) * mm, "radius": 1.56 * mm});
            skCircle(sketch, "E33.1.15.0", {"center": v(12.51, 55.84) * mm, "radius": 1.56 * mm});
            skCircle(sketch, "E33.2.15.0", {"center": v(4.5, 57.04) * mm, "radius": 1.56 * mm});
            skCircle(sketch, "E33.1.16.0", {"center": v(-4.5, 57.04) * mm, "radius": 1.56 * mm});
            skCircle(sketch, "E33.2.16.0", {"center": v(-12.51, 55.84) * mm, "radius": 1.56 * mm});
            skCircle(sketch, "E33.1.17.0", {"center": v(-21.11, 53.18) * mm, "radius": 1.56 * mm});
            skCircle(sketch, "E33.2.17.0", {"center": v(-28.41, 49.67) * mm, "radius": 1.56 * mm});
            skCircle(sketch, "E33.1.18.0", {"center": v(-35.85, 44.6) * mm, "radius": 1.56 * mm});
            skCircle(sketch, "E33.2.18.0", {"center": v(-41.8, 39.09) * mm, "radius": 1.56 * mm});
            skCircle(sketch, "E33.1.19.0", {"center": v(-47.4, 32.05) * mm, "radius": 1.56 * mm});
            skCircle(sketch, "E33.2.19.0", {"center": v(-51.46, 25.03) * mm, "radius": 1.56 * mm});
            skCircle(sketch, "E33.1.20.0", {"center": v(-54.74, 16.65) * mm, "radius": 1.56 * mm});
            skCircle(sketch, "E33.2.20.0", {"center": v(-56.55, 8.75) * mm, "radius": 1.56 * mm});
            skSolve(sketch);
        }
        {
            var Q0;
            Q0 = qSketchRegion(id + "F6", true);
            extrude(context, id + "F7", {"entities" : qUnion([Q0]), "operationType" : NewBodyOperationType.REMOVE, "oppositeDirection" : true, "depth" : 25 * mm, "offsetDistance" : 25 * mm});
        }
        {
            var Q0;
            Q0=makeQuery(id+"F1.opExtrude","CAP_FACE",FACE,{"disambiguationData":[OSD([sQuery(id+"F0.wireOp",EDGE,"E0"),sQuery(id+"F0.wireOp",EDGE,"E1"),sQuery(id+"F0.wireOp",EDGE,"E6"),sQuery(id+"F0.wireOp",EDGE,"E7"),sQuery(id+"F0.wireOp",EDGE,"E8"),sQuery(id+"F0.wireOp",EDGE,"E9"),sQuery(id+"F0.wireOp",EDGE,"E10"),sQuery(id+"F0.wireOp",EDGE,"E11"),sQuery(id+"F0.wireOp",EDGE,"E12"),sQuery(id+"F0.wireOp",EDGE,"E13.1.0"),sQuery(id+"F0.wireOp",EDGE,"E13.1.1"),sQuery(id+"F0.wireOp",EDGE,"E13.1.2"),sQuery(id+"F0.wireOp",EDGE,"E13.1.3"),sQuery(id+"F0.wireOp",EDGE,"E13.2.0"),sQuery(id+"F0.wireOp",EDGE,"E13.2.1"),sQuery(id+"F0.wireOp",EDGE,"E13.2.2"),sQuery(id+"F0.wireOp",EDGE,"E13.2.3"),sQuery(id+"F0.wireOp",EDGE,"E14.1.3.0"),sQuery(id+"F0.wireOp",EDGE,"E14.2.3.0"),sQuery(id+"F0.wireOp",EDGE,"E14.4.3.0"),sQuery(id+"F0.wireOp",EDGE,"E14.6.3.0"),sQuery(id+"F0.wireOp",EDGE,"E14.1.4.0"),sQuery(id+"F0.wireOp",EDGE,"E14.2.4.0"),sQuery(id+"F0.wireOp",EDGE,"E14.4.4.0"),sQuery(id+"F0.wireOp",EDGE,"E14.6.4.0"),sQuery(id+"F0.wireOp",EDGE,"E14.1.5.0"),sQuery(id+"F0.wireOp",EDGE,"E14.2.5.0"),sQuery(id+"F0.wireOp",EDGE,"E14.4.5.0"),sQuery(id+"F0.wireOp",EDGE,"E14.6.5.0"),sQuery(id+"F0.wireOp",EDGE,"E14.1.6.0"),sQuery(id+"F0.wireOp",EDGE,"E14.2.6.0"),sQuery(id+"F0.wireOp",EDGE,"E14.4.6.0"),sQuery(id+"F0.wireOp",EDGE,"E14.6.6.0"),sQuery(id+"F0.wireOp",EDGE,"E14.1.7.0"),sQuery(id+"F0.wireOp",EDGE,"E14.2.7.0"),sQuery(id+"F0.wireOp",EDGE,"E14.4.7.0"),sQuery(id+"F0.wireOp",EDGE,"E14.6.7.0"),sQuery(id+"F0.wireOp",EDGE,"E14.1.8.0"),sQuery(id+"F0.wireOp",EDGE,"E14.2.8.0"),sQuery(id+"F0.wireOp",EDGE,"E14.4.8.0"),sQuery(id+"F0.wireOp",EDGE,"E14.6.8.0"),sQuery(id+"F0.wireOp",EDGE,"E14.1.9.0"),sQuery(id+"F0.wireOp",EDGE,"E14.2.9.0"),sQuery(id+"F0.wireOp",EDGE,"E14.4.9.0"),sQuery(id+"F0.wireOp",EDGE,"E14.6.9.0"),sQuery(id+"F0.wireOp",EDGE,"E14.1.10.0"),sQuery(id+"F0.wireOp",EDGE,"E14.2.10.0"),sQuery(id+"F0.wireOp",EDGE,"E14.4.10.0"),sQuery(id+"F0.wireOp",EDGE,"E14.6.10.0"),sQuery(id+"F0.wireOp",EDGE,"E14.1.11.0"),sQuery(id+"F0.wireOp",EDGE,"E14.2.11.0"),sQuery(id+"F0.wireOp",EDGE,"E14.4.11.0"),sQuery(id+"F0.wireOp",EDGE,"E14.6.11.0"),sQuery(id+"F0.wireOp",EDGE,"E14.1.12.0"),sQuery(id+"F0.wireOp",EDGE,"E14.2.12.0"),sQuery(id+"F0.wireOp",EDGE,"E14.4.12.0"),sQuery(id+"F0.wireOp",EDGE,"E14.6.12.0"),sQuery(id+"F0.wireOp",EDGE,"E14.1.13.0"),sQuery(id+"F0.wireOp",EDGE,"E14.2.13.0"),sQuery(id+"F0.wireOp",EDGE,"E14.4.13.0"),sQuery(id+"F0.wireOp",EDGE,"E14.6.13.0"),sQuery(id+"F0.wireOp",EDGE,"E14.1.14.0"),sQuery(id+"F0.wireOp",EDGE,"E14.2.14.0"),sQuery(id+"F0.wireOp",EDGE,"E14.4.14.0"),sQuery(id+"F0.wireOp",EDGE,"E14.6.14.0"),sQuery(id+"F0.wireOp",EDGE,"E14.1.15.0"),sQuery(id+"F0.wireOp",EDGE,"E14.2.15.0"),sQuery(id+"F0.wireOp",EDGE,"E14.4.15.0"),sQuery(id+"F0.wireOp",EDGE,"E14.6.15.0"),sQuery(id+"F0.wireOp",EDGE,"E14.1.16.0"),sQuery(id+"F0.wireOp",EDGE,"E14.2.16.0"),sQuery(id+"F0.wireOp",EDGE,"E14.4.16.0"),sQuery(id+"F0.wireOp",EDGE,"E14.6.16.0"),sQuery(id+"F0.wireOp",EDGE,"E14.1.17.0"),sQuery(id+"F0.wireOp",EDGE,"E14.2.17.0"),sQuery(id+"F0.wireOp",EDGE,"E14.4.17.0"),sQuery(id+"F0.wireOp",EDGE,"E14.6.17.0"),sQuery(id+"F0.wireOp",EDGE,"E14.1.18.0"),sQuery(id+"F0.wireOp",EDGE,"E14.2.18.0"),sQuery(id+"F0.wireOp",EDGE,"E14.4.18.0"),sQuery(id+"F0.wireOp",EDGE,"E14.6.18.0"),sQuery(id+"F0.wireOp",EDGE,"E14.1.19.0"),sQuery(id+"F0.wireOp",EDGE,"E14.2.19.0"),sQuery(id+"F0.wireOp",EDGE,"E14.4.19.0"),sQuery(id+"F0.wireOp",EDGE,"E14.6.19.0"),sQuery(id+"F0.wireOp",EDGE,"E14.1.20.0"),sQuery(id+"F0.wireOp",EDGE,"E14.2.20.0"),sQuery(id+"F0.wireOp",EDGE,"E14.4.20.0"),sQuery(id+"F0.wireOp",EDGE,"E14.6.20.0"),sQuery(id+"F0.wireOp",EDGE,"E16"),sQuery(id+"F0.wireOp",EDGE,"E17"),sQuery(id+"F0.wireOp",EDGE,"E18"),sQuery(id+"F0.wireOp",EDGE,"E19"),sQuery(id+"F0.wireOp",EDGE,"E20"),sQuery(id+"F0.wireOp",EDGE,"E21.1.0"),sQuery(id+"F0.wireOp",EDGE,"E21.1.1"),sQuery(id+"F0.wireOp",EDGE,"E21.1.2"),sQuery(id+"F0.wireOp",EDGE,"E21.1.3"),sQuery(id+"F0.wireOp",EDGE,"E21.1.4"),sQuery(id+"F0.wireOp",EDGE,"E21.1.5"),sQuery(id+"F0.wireOp",EDGE,"E21.1.6"),sQuery(id+"F0.wireOp",EDGE,"E21.1.7"),sQuery(id+"F0.wireOp",EDGE,"E21.2.0"),sQuery(id+"F0.wireOp",EDGE,"E21.2.1"),sQuery(id+"F0.wireOp",EDGE,"E21.2.2"),sQuery(id+"F0.wireOp",EDGE,"E21.2.3"),sQuery(id+"F0.wireOp",EDGE,"E21.2.4"),sQuery(id+"F0.wireOp",EDGE,"E21.2.5"),sQuery(id+"F0.wireOp",EDGE,"E21.2.6"),sQuery(id+"F0.wireOp",EDGE,"E21.2.7")])],"isStart":false});
            var sketch = newSketch(context, id + "F8", { "sketchPlane" : qUnion([Q0])});
            skLineSegment(sketch, "E34", {"start": v(0, 0) * mm, "end": v(32.22, 47.26) * mm, "construction": true});
            skCircle(sketch, "E35", {"center": v(16.9, 24.79) * mm, "radius": 2.25 * mm});
            skCircle(sketch, "E36.1.0", {"center": v(-29.92, 2.24) * mm, "radius": 2.25 * mm, "construction": true});
            skCircle(sketch, "E36.2.0", {"center": v(13.02, -27.03) * mm, "radius": 2.25 * mm, "construction": true});
            skPoint(sketch, "E36.center", {"position": v(0, 0) * mm});
            skCircle(sketch, "E37.1.0", {"center": v(8.84, 28.67) * mm, "radius": 2.25 * mm});
            skCircle(sketch, "E37.2.0", {"center": v(0, 30) * mm, "radius": 2.25 * mm});
            skCircle(sketch, "E37.3.0", {"center": v(-8.84, 28.67) * mm, "radius": 2.25 * mm});
            skCircle(sketch, "E37.4.0", {"center": v(-16.9, 24.79) * mm, "radius": 2.25 * mm});
            skCircle(sketch, "E37.5.0", {"center": v(-23.45, 18.7) * mm, "radius": 2.25 * mm});
            skCircle(sketch, "E37.6.0", {"center": v(-27.93, 10.96) * mm, "radius": 2.25 * mm});
            skCircle(sketch, "E37.7.0", {"center": v(-29.92, 2.24) * mm, "radius": 2.25 * mm});
            skCircle(sketch, "E37.8.0", {"center": v(-29.25, -6.68) * mm, "radius": 2.25 * mm});
            skCircle(sketch, "E37.9.0", {"center": v(-25.98, -15) * mm, "radius": 2.25 * mm});
            skCircle(sketch, "E37.10.0", {"center": v(-20.4, -22) * mm, "radius": 2.25 * mm});
            skCircle(sketch, "E37.11.0", {"center": v(-13.02, -27.03) * mm, "radius": 2.25 * mm});
            skCircle(sketch, "E37.12.0", {"center": v(-4.47, -29.66) * mm, "radius": 2.25 * mm});
            skCircle(sketch, "E37.13.0", {"center": v(4.47, -29.66) * mm, "radius": 2.25 * mm});
            skCircle(sketch, "E37.14.0", {"center": v(13.02, -27.03) * mm, "radius": 2.25 * mm});
            skCircle(sketch, "E37.15.0", {"center": v(20.4, -22) * mm, "radius": 2.25 * mm});
            skCircle(sketch, "E37.16.0", {"center": v(25.98, -15) * mm, "radius": 2.25 * mm});
            skCircle(sketch, "E37.17.0", {"center": v(29.25, -6.68) * mm, "radius": 2.25 * mm});
            skCircle(sketch, "E37.18.0", {"center": v(29.92, 2.24) * mm, "radius": 2.25 * mm});
            skCircle(sketch, "E37.19.0", {"center": v(27.93, 10.96) * mm, "radius": 2.25 * mm});
            skCircle(sketch, "E37.20.0", {"center": v(23.45, 18.7) * mm, "radius": 2.25 * mm});
            skSolve(sketch);
        }
        {
            var Q0;
            Q0 = qSketchRegion(id + "F8", true);
            extrude(context, id + "F9", {"entities" : qUnion([Q0]), "operationType" : NewBodyOperationType.REMOVE, "oppositeDirection" : true, "depth" : 25 * mm, "offsetDistance" : 25 * mm});
        }
        {
            var Q0;
            Q0=makeQuery(id+"F1.opExtrude","CAP_FACE",FACE,{"disambiguationData":[OSD([sQuery(id+"F0.wireOp",EDGE,"E0"),sQuery(id+"F0.wireOp",EDGE,"E1"),sQuery(id+"F0.wireOp",EDGE,"E6"),sQuery(id+"F0.wireOp",EDGE,"E7"),sQuery(id+"F0.wireOp",EDGE,"E8"),sQuery(id+"F0.wireOp",EDGE,"E9"),sQuery(id+"F0.wireOp",EDGE,"E10"),sQuery(id+"F0.wireOp",EDGE,"E11"),sQuery(id+"F0.wireOp",EDGE,"E12"),sQuery(id+"F0.wireOp",EDGE,"E13.1.0"),sQuery(id+"F0.wireOp",EDGE,"E13.1.1"),sQuery(id+"F0.wireOp",EDGE,"E13.1.2"),sQuery(id+"F0.wireOp",EDGE,"E13.1.3"),sQuery(id+"F0.wireOp",EDGE,"E13.2.0"),sQuery(id+"F0.wireOp",EDGE,"E13.2.1"),sQuery(id+"F0.wireOp",EDGE,"E13.2.2"),sQuery(id+"F0.wireOp",EDGE,"E13.2.3"),sQuery(id+"F0.wireOp",EDGE,"E14.1.3.0"),sQuery(id+"F0.wireOp",EDGE,"E14.2.3.0"),sQuery(id+"F0.wireOp",EDGE,"E14.4.3.0"),sQuery(id+"F0.wireOp",EDGE,"E14.6.3.0"),sQuery(id+"F0.wireOp",EDGE,"E14.1.4.0"),sQuery(id+"F0.wireOp",EDGE,"E14.2.4.0"),sQuery(id+"F0.wireOp",EDGE,"E14.4.4.0"),sQuery(id+"F0.wireOp",EDGE,"E14.6.4.0"),sQuery(id+"F0.wireOp",EDGE,"E14.1.5.0"),sQuery(id+"F0.wireOp",EDGE,"E14.2.5.0"),sQuery(id+"F0.wireOp",EDGE,"E14.4.5.0"),sQuery(id+"F0.wireOp",EDGE,"E14.6.5.0"),sQuery(id+"F0.wireOp",EDGE,"E14.1.6.0"),sQuery(id+"F0.wireOp",EDGE,"E14.2.6.0"),sQuery(id+"F0.wireOp",EDGE,"E14.4.6.0"),sQuery(id+"F0.wireOp",EDGE,"E14.6.6.0"),sQuery(id+"F0.wireOp",EDGE,"E14.1.7.0"),sQuery(id+"F0.wireOp",EDGE,"E14.2.7.0"),sQuery(id+"F0.wireOp",EDGE,"E14.4.7.0"),sQuery(id+"F0.wireOp",EDGE,"E14.6.7.0"),sQuery(id+"F0.wireOp",EDGE,"E14.1.8.0"),sQuery(id+"F0.wireOp",EDGE,"E14.2.8.0"),sQuery(id+"F0.wireOp",EDGE,"E14.4.8.0"),sQuery(id+"F0.wireOp",EDGE,"E14.6.8.0"),sQuery(id+"F0.wireOp",EDGE,"E14.1.9.0"),sQuery(id+"F0.wireOp",EDGE,"E14.2.9.0"),sQuery(id+"F0.wireOp",EDGE,"E14.4.9.0"),sQuery(id+"F0.wireOp",EDGE,"E14.6.9.0"),sQuery(id+"F0.wireOp",EDGE,"E14.1.10.0"),sQuery(id+"F0.wireOp",EDGE,"E14.2.10.0"),sQuery(id+"F0.wireOp",EDGE,"E14.4.10.0"),sQuery(id+"F0.wireOp",EDGE,"E14.6.10.0"),sQuery(id+"F0.wireOp",EDGE,"E14.1.11.0"),sQuery(id+"F0.wireOp",EDGE,"E14.2.11.0"),sQuery(id+"F0.wireOp",EDGE,"E14.4.11.0"),sQuery(id+"F0.wireOp",EDGE,"E14.6.11.0"),sQuery(id+"F0.wireOp",EDGE,"E14.1.12.0"),sQuery(id+"F0.wireOp",EDGE,"E14.2.12.0"),sQuery(id+"F0.wireOp",EDGE,"E14.4.12.0"),sQuery(id+"F0.wireOp",EDGE,"E14.6.12.0"),sQuery(id+"F0.wireOp",EDGE,"E14.1.13.0"),sQuery(id+"F0.wireOp",EDGE,"E14.2.13.0"),sQuery(id+"F0.wireOp",EDGE,"E14.4.13.0"),sQuery(id+"F0.wireOp",EDGE,"E14.6.13.0"),sQuery(id+"F0.wireOp",EDGE,"E14.1.14.0"),sQuery(id+"F0.wireOp",EDGE,"E14.2.14.0"),sQuery(id+"F0.wireOp",EDGE,"E14.4.14.0"),sQuery(id+"F0.wireOp",EDGE,"E14.6.14.0"),sQuery(id+"F0.wireOp",EDGE,"E14.1.15.0"),sQuery(id+"F0.wireOp",EDGE,"E14.2.15.0"),sQuery(id+"F0.wireOp",EDGE,"E14.4.15.0"),sQuery(id+"F0.wireOp",EDGE,"E14.6.15.0"),sQuery(id+"F0.wireOp",EDGE,"E14.1.16.0"),sQuery(id+"F0.wireOp",EDGE,"E14.2.16.0"),sQuery(id+"F0.wireOp",EDGE,"E14.4.16.0"),sQuery(id+"F0.wireOp",EDGE,"E14.6.16.0"),sQuery(id+"F0.wireOp",EDGE,"E14.1.17.0"),sQuery(id+"F0.wireOp",EDGE,"E14.2.17.0"),sQuery(id+"F0.wireOp",EDGE,"E14.4.17.0"),sQuery(id+"F0.wireOp",EDGE,"E14.6.17.0"),sQuery(id+"F0.wireOp",EDGE,"E14.1.18.0"),sQuery(id+"F0.wireOp",EDGE,"E14.2.18.0"),sQuery(id+"F0.wireOp",EDGE,"E14.4.18.0"),sQuery(id+"F0.wireOp",EDGE,"E14.6.18.0"),sQuery(id+"F0.wireOp",EDGE,"E14.1.19.0"),sQuery(id+"F0.wireOp",EDGE,"E14.2.19.0"),sQuery(id+"F0.wireOp",EDGE,"E14.4.19.0"),sQuery(id+"F0.wireOp",EDGE,"E14.6.19.0"),sQuery(id+"F0.wireOp",EDGE,"E14.1.20.0"),sQuery(id+"F0.wireOp",EDGE,"E14.2.20.0"),sQuery(id+"F0.wireOp",EDGE,"E14.4.20.0"),sQuery(id+"F0.wireOp",EDGE,"E14.6.20.0"),sQuery(id+"F0.wireOp",EDGE,"E16"),sQuery(id+"F0.wireOp",EDGE,"E17"),sQuery(id+"F0.wireOp",EDGE,"E18"),sQuery(id+"F0.wireOp",EDGE,"E19"),sQuery(id+"F0.wireOp",EDGE,"E20"),sQuery(id+"F0.wireOp",EDGE,"E21.1.0"),sQuery(id+"F0.wireOp",EDGE,"E21.1.1"),sQuery(id+"F0.wireOp",EDGE,"E21.1.2"),sQuery(id+"F0.wireOp",EDGE,"E21.1.3"),sQuery(id+"F0.wireOp",EDGE,"E21.1.4"),sQuery(id+"F0.wireOp",EDGE,"E21.1.5"),sQuery(id+"F0.wireOp",EDGE,"E21.1.6"),sQuery(id+"F0.wireOp",EDGE,"E21.1.7"),sQuery(id+"F0.wireOp",EDGE,"E21.2.0"),sQuery(id+"F0.wireOp",EDGE,"E21.2.1"),sQuery(id+"F0.wireOp",EDGE,"E21.2.2"),sQuery(id+"F0.wireOp",EDGE,"E21.2.3"),sQuery(id+"F0.wireOp",EDGE,"E21.2.4"),sQuery(id+"F0.wireOp",EDGE,"E21.2.5"),sQuery(id+"F0.wireOp",EDGE,"E21.2.6"),sQuery(id+"F0.wireOp",EDGE,"E21.2.7")])],"isStart":false});
            var sketch = newSketch(context, id + "F10", { "sketchPlane" : qUnion([Q0])});
            skArc(sketch, "E38", {"start": v(44.69, -6.07) * mm, "mid": v(44.97, -3.37) * mm, "end": v(45.1, -0.66) * mm});
            skArc(sketch, "E39", {"start": v(37.95, -5.15) * mm, "mid": v(38.2, -2.86) * mm, "end": v(38.3, -0.56) * mm});
            skArc(sketch, "E40", {"start": v(34.98, -4.75) * mm, "mid": v(35.2, -2.64) * mm, "end": v(35.3, -0.52) * mm});
            skLineSegment(sketch, "E41", {"start": v(0, 0) * mm, "end": v(0.1, -0.01) * mm, "construction": true});
            skLineSegment(sketch, "E42", {"start": v(-0.78, 0) * mm, "end": v(0.1, -0.01) * mm, "construction": true});
            skLineSegment(sketch, "E43.trimOffspring", {"start": v(48.9, -0.71) * mm, "end": v(51.9, -0.76) * mm});
            skLineSegment(sketch, "E44.trimOffspring", {"start": v(48.46, -6.58) * mm, "end": v(51.43, -6.98) * mm});
            skLineSegment(sketch, "E45.trimOffspring", {"start": v(41.72, -5.67) * mm, "end": v(44.69, -6.07) * mm});
            skLineSegment(sketch, "E46.trimOffspring", {"start": v(42.1, -0.62) * mm, "end": v(45.1, -0.66) * mm});
            skLineSegment(sketch, "E47.trimOffspring", {"start": v(34.98, -4.75) * mm, "end": v(37.95, -5.15) * mm});
            skLineSegment(sketch, "E48.trimOffspring", {"start": v(35.3, -0.52) * mm, "end": v(38.3, -0.56) * mm});
            skLineSegment(sketch, "E49.1.0", {"start": v(46.93, 13.73) * mm, "end": v(49.81, 14.57) * mm});
            skArc(sketch, "E49.1.1", {"start": v(37.78, 6.26) * mm, "mid": v(37.34, 8.52) * mm, "end": v(36.76, 10.75) * mm});
            skArc(sketch, "E49.1.2", {"start": v(34.83, 5.77) * mm, "mid": v(34.42, 7.85) * mm, "end": v(33.88, 9.9) * mm});
            skLineSegment(sketch, "E49.1.3", {"start": v(40.4, 11.82) * mm, "end": v(43.29, 12.66) * mm});
            skLineSegment(sketch, "E49.1.4", {"start": v(41.53, 6.88) * mm, "end": v(44.5, 7.37) * mm});
            skArc(sketch, "E49.1.5", {"start": v(41.53, 6.88) * mm, "mid": v(41.04, 9.37) * mm, "end": v(40.4, 11.82) * mm});
            skLineSegment(sketch, "E49.1.6", {"start": v(33.88, 9.9) * mm, "end": v(36.76, 10.75) * mm});
            skArc(sketch, "E49.1.7", {"start": v(48.24, 8) * mm, "mid": v(47.67, 10.88) * mm, "end": v(46.93, 13.73) * mm});
            skArc(sketch, "E49.1.8", {"start": v(44.5, 7.37) * mm, "mid": v(43.97, 10.04) * mm, "end": v(43.29, 12.66) * mm});
            skArc(sketch, "E49.1.9", {"start": v(51.2, 8.48) * mm, "mid": v(50.6, 11.55) * mm, "end": v(49.81, 14.57) * mm});
            skLineSegment(sketch, "E49.1.10", {"start": v(34.83, 5.77) * mm, "end": v(37.78, 6.26) * mm});
            skLineSegment(sketch, "E49.1.11", {"start": v(48.24, 8) * mm, "end": v(51.2, 8.48) * mm});
            skLineSegment(sketch, "E49.2.0", {"start": v(40.8, 26.95) * mm, "end": v(43.3, 28.6) * mm});
            skArc(sketch, "E49.2.1", {"start": v(34.26, 17.12) * mm, "mid": v(33.17, 19.15) * mm, "end": v(31.96, 21.1) * mm});
            skArc(sketch, "E49.2.2", {"start": v(31.58, 15.78) * mm, "mid": v(30.57, 17.65) * mm, "end": v(29.46, 19.45) * mm});
            skLineSegment(sketch, "E49.2.3", {"start": v(35.13, 23.2) * mm, "end": v(37.63, 24.86) * mm});
            skLineSegment(sketch, "E49.2.4", {"start": v(37.66, 18.82) * mm, "end": v(40.34, 20.16) * mm});
            skArc(sketch, "E49.2.5", {"start": v(37.66, 18.82) * mm, "mid": v(36.46, 21.05) * mm, "end": v(35.13, 23.2) * mm});
            skLineSegment(sketch, "E49.2.6", {"start": v(29.46, 19.45) * mm, "end": v(31.96, 21.1) * mm});
            skArc(sketch, "E49.2.7", {"start": v(43.74, 21.86) * mm, "mid": v(42.35, 24.45) * mm, "end": v(40.8, 26.95) * mm});
            skArc(sketch, "E49.2.8", {"start": v(40.34, 20.16) * mm, "mid": v(39.06, 22.55) * mm, "end": v(37.63, 24.86) * mm});
            skArc(sketch, "E49.2.9", {"start": v(46.43, 23.2) * mm, "mid": v(44.95, 25.95) * mm, "end": v(43.3, 28.6) * mm});
            skLineSegment(sketch, "E49.2.10", {"start": v(31.58, 15.78) * mm, "end": v(34.26, 17.12) * mm});
            skLineSegment(sketch, "E49.2.11", {"start": v(43.74, 21.86) * mm, "end": v(46.43, 23.2) * mm});
            skArc(sketch, "E50.3.3.0", {"start": v(27.7, 26.46) * mm, "mid": v(26.05, 28.07) * mm, "end": v(24.32, 29.6) * mm});
            skArc(sketch, "E50.7.3.0", {"start": v(25.52, 24.39) * mm, "mid": v(24.01, 25.88) * mm, "end": v(22.41, 27.27) * mm});
            skLineSegment(sketch, "E50.9.3.0", {"start": v(31.04, 37.78) * mm, "end": v(32.95, 40.1) * mm});
            skLineSegment(sketch, "E50.11.3.0", {"start": v(26.73, 32.53) * mm, "end": v(28.63, 34.85) * mm});
            skLineSegment(sketch, "E50.14.3.0", {"start": v(30.44, 29.08) * mm, "end": v(32.6, 31.16) * mm});
            skArc(sketch, "E50.17.3.0", {"start": v(30.44, 29.08) * mm, "mid": v(28.64, 30.86) * mm, "end": v(26.73, 32.53) * mm});
            skLineSegment(sketch, "E50.21.3.0", {"start": v(22.41, 27.27) * mm, "end": v(24.32, 29.6) * mm});
            skArc(sketch, "E50.24.3.0", {"start": v(35.36, 33.78) * mm, "mid": v(33.26, 35.85) * mm, "end": v(31.04, 37.78) * mm});
            skArc(sketch, "E50.28.3.0", {"start": v(32.6, 31.16) * mm, "mid": v(30.68, 33.06) * mm, "end": v(28.63, 34.85) * mm});
            skArc(sketch, "E50.32.3.0", {"start": v(37.53, 35.85) * mm, "mid": v(35.3, 38.05) * mm, "end": v(32.95, 40.1) * mm});
            skLineSegment(sketch, "E50.36.3.0", {"start": v(25.52, 24.39) * mm, "end": v(27.7, 26.46) * mm});
            skLineSegment(sketch, "E50.39.3.0", {"start": v(35.36, 33.78) * mm, "end": v(37.53, 35.85) * mm});
            skArc(sketch, "E50.3.4.0", {"start": v(18.66, 33.44) * mm, "mid": v(16.62, 34.5) * mm, "end": v(14.51, 35.44) * mm});
            skArc(sketch, "E50.7.4.0", {"start": v(17.2, 30.83) * mm, "mid": v(15.32, 31.8) * mm, "end": v(13.38, 32.67) * mm});
            skLineSegment(sketch, "E50.9.4.0", {"start": v(18.53, 45.25) * mm, "end": v(19.66, 48.03) * mm});
            skLineSegment(sketch, "E50.11.4.0", {"start": v(15.95, 38.96) * mm, "end": v(17.09, 41.74) * mm});
            skLineSegment(sketch, "E50.14.4.0", {"start": v(20.52, 36.76) * mm, "end": v(21.98, 39.38) * mm});
            skArc(sketch, "E50.17.4.0", {"start": v(20.52, 36.76) * mm, "mid": v(18.27, 37.93) * mm, "end": v(15.95, 38.96) * mm});
            skLineSegment(sketch, "E50.21.4.0", {"start": v(13.38, 32.67) * mm, "end": v(14.51, 35.44) * mm});
            skArc(sketch, "E50.24.4.0", {"start": v(23.83, 42.7) * mm, "mid": v(21.22, 44.06) * mm, "end": v(18.53, 45.25) * mm});
            skArc(sketch, "E50.28.4.0", {"start": v(21.98, 39.38) * mm, "mid": v(19.57, 40.63) * mm, "end": v(17.09, 41.74) * mm});
            skArc(sketch, "E50.32.4.0", {"start": v(25.3, 45.32) * mm, "mid": v(22.52, 46.76) * mm, "end": v(19.66, 48.03) * mm});
            skLineSegment(sketch, "E50.36.4.0", {"start": v(17.2, 30.83) * mm, "end": v(18.66, 33.44) * mm});
            skLineSegment(sketch, "E50.39.4.0", {"start": v(23.83, 42.7) * mm, "end": v(25.3, 45.32) * mm});
            skArc(sketch, "E50.3.5.0", {"start": v(7.98, 37.46) * mm, "mid": v(5.7, 37.87) * mm, "end": v(3.42, 38.15) * mm});
            skArc(sketch, "E50.7.5.0", {"start": v(7.35, 34.53) * mm, "mid": v(5.26, 34.9) * mm, "end": v(3.16, 35.16) * mm});
            skLineSegment(sketch, "E50.9.5.0", {"start": v(4.37, 48.7) * mm, "end": v(4.63, 51.7) * mm});
            skLineSegment(sketch, "E50.11.5.0", {"start": v(3.76, 41.93) * mm, "end": v(4.03, 44.92) * mm});
            skLineSegment(sketch, "E50.14.5.0", {"start": v(8.77, 41.18) * mm, "end": v(9.4, 44.11) * mm});
            skArc(sketch, "E50.17.5.0", {"start": v(8.77, 41.18) * mm, "mid": v(6.28, 41.63) * mm, "end": v(3.76, 41.93) * mm});
            skLineSegment(sketch, "E50.21.5.0", {"start": v(3.16, 35.16) * mm, "end": v(3.42, 38.15) * mm});
            skArc(sketch, "E50.24.5.0", {"start": v(10.18, 47.83) * mm, "mid": v(7.29, 48.35) * mm, "end": v(4.37, 48.7) * mm});
            skArc(sketch, "E50.28.5.0", {"start": v(9.4, 44.11) * mm, "mid": v(6.72, 44.6) * mm, "end": v(4.03, 44.92) * mm});
            skArc(sketch, "E50.32.5.0", {"start": v(10.8, 50.76) * mm, "mid": v(7.74, 51.32) * mm, "end": v(4.63, 51.7) * mm});
            skLineSegment(sketch, "E50.36.5.0", {"start": v(7.35, 34.53) * mm, "end": v(7.98, 37.46) * mm});
            skLineSegment(sketch, "E50.39.5.0", {"start": v(10.18, 47.83) * mm, "end": v(10.8, 50.76) * mm});
            skArc(sketch, "E50.3.6.0", {"start": v(-3.42, 38.15) * mm, "mid": v(-5.7, 37.87) * mm, "end": v(-7.97, 37.46) * mm});
            skArc(sketch, "E50.7.6.0", {"start": v(-3.15, 35.16) * mm, "mid": v(-5.26, 34.9) * mm, "end": v(-7.35, 34.53) * mm});
            skLineSegment(sketch, "E50.9.6.0", {"start": v(-10.18, 47.83) * mm, "end": v(-10.8, 50.76) * mm});
            skLineSegment(sketch, "E50.11.6.0", {"start": v(-8.77, 41.18) * mm, "end": v(-9.4, 44.11) * mm});
            skLineSegment(sketch, "E50.14.6.0", {"start": v(-3.76, 41.93) * mm, "end": v(-4.03, 44.92) * mm});
            skArc(sketch, "E50.17.6.0", {"start": v(-3.76, 41.93) * mm, "mid": v(-6.27, 41.63) * mm, "end": v(-8.77, 41.18) * mm});
            skLineSegment(sketch, "E50.21.6.0", {"start": v(-7.35, 34.53) * mm, "end": v(-7.97, 37.46) * mm});
            skArc(sketch, "E50.24.6.0", {"start": v(-4.37, 48.7) * mm, "mid": v(-7.29, 48.35) * mm, "end": v(-10.18, 47.83) * mm});
            skArc(sketch, "E50.28.6.0", {"start": v(-4.03, 44.92) * mm, "mid": v(-6.72, 44.6) * mm, "end": v(-9.4, 44.11) * mm});
            skArc(sketch, "E50.32.6.0", {"start": v(-4.63, 51.7) * mm, "mid": v(-7.74, 51.32) * mm, "end": v(-10.8, 50.76) * mm});
            skLineSegment(sketch, "E50.36.6.0", {"start": v(-3.15, 35.16) * mm, "end": v(-3.42, 38.15) * mm});
            skLineSegment(sketch, "E50.39.6.0", {"start": v(-4.37, 48.7) * mm, "end": v(-4.63, 51.7) * mm});
            skArc(sketch, "E50.3.7.0", {"start": v(-14.51, 35.44) * mm, "mid": v(-16.62, 34.5) * mm, "end": v(-18.66, 33.45) * mm});
            skArc(sketch, "E50.7.7.0", {"start": v(-13.38, 32.67) * mm, "mid": v(-15.31, 31.8) * mm, "end": v(-17.2, 30.83) * mm});
            skLineSegment(sketch, "E50.9.7.0", {"start": v(-23.83, 42.7) * mm, "end": v(-25.3, 45.32) * mm});
            skLineSegment(sketch, "E50.11.7.0", {"start": v(-20.51, 36.76) * mm, "end": v(-21.98, 39.38) * mm});
            skLineSegment(sketch, "E50.14.7.0", {"start": v(-15.95, 38.96) * mm, "end": v(-17.09, 41.74) * mm});
            skArc(sketch, "E50.17.7.0", {"start": v(-15.95, 38.96) * mm, "mid": v(-18.27, 37.93) * mm, "end": v(-20.51, 36.76) * mm});
            skLineSegment(sketch, "E50.21.7.0", {"start": v(-17.2, 30.83) * mm, "end": v(-18.66, 33.45) * mm});
            skArc(sketch, "E50.24.7.0", {"start": v(-18.53, 45.25) * mm, "mid": v(-21.22, 44.06) * mm, "end": v(-23.83, 42.7) * mm});
            skArc(sketch, "E50.28.7.0", {"start": v(-17.09, 41.74) * mm, "mid": v(-19.57, 40.63) * mm, "end": v(-21.98, 39.38) * mm});
            skArc(sketch, "E50.32.7.0", {"start": v(-19.66, 48.03) * mm, "mid": v(-22.52, 46.76) * mm, "end": v(-25.3, 45.32) * mm});
            skLineSegment(sketch, "E50.36.7.0", {"start": v(-13.38, 32.67) * mm, "end": v(-14.51, 35.44) * mm});
            skLineSegment(sketch, "E50.39.7.0", {"start": v(-18.53, 45.25) * mm, "end": v(-19.66, 48.03) * mm});
            skArc(sketch, "E50.3.8.0", {"start": v(-24.31, 29.6) * mm, "mid": v(-26.05, 28.08) * mm, "end": v(-27.7, 26.46) * mm});
            skArc(sketch, "E50.7.8.0", {"start": v(-22.4, 27.27) * mm, "mid": v(-24, 25.88) * mm, "end": v(-25.52, 24.39) * mm});
            skLineSegment(sketch, "E50.9.8.0", {"start": v(-35.36, 33.78) * mm, "end": v(-37.53, 35.85) * mm});
            skLineSegment(sketch, "E50.11.8.0", {"start": v(-30.44, 29.08) * mm, "end": v(-32.6, 31.16) * mm});
            skLineSegment(sketch, "E50.14.8.0", {"start": v(-26.73, 32.53) * mm, "end": v(-28.63, 34.85) * mm});
            skArc(sketch, "E50.17.8.0", {"start": v(-26.73, 32.53) * mm, "mid": v(-28.63, 30.86) * mm, "end": v(-30.44, 29.08) * mm});
            skLineSegment(sketch, "E50.21.8.0", {"start": v(-25.52, 24.39) * mm, "end": v(-27.7, 26.46) * mm});
            skArc(sketch, "E50.24.8.0", {"start": v(-31.04, 37.78) * mm, "mid": v(-33.26, 35.85) * mm, "end": v(-35.36, 33.78) * mm});
            skArc(sketch, "E50.28.8.0", {"start": v(-28.63, 34.85) * mm, "mid": v(-30.68, 33.06) * mm, "end": v(-32.6, 31.16) * mm});
            skArc(sketch, "E50.32.8.0", {"start": v(-32.95, 40.1) * mm, "mid": v(-35.3, 38.05) * mm, "end": v(-37.53, 35.85) * mm});
            skLineSegment(sketch, "E50.36.8.0", {"start": v(-22.4, 27.27) * mm, "end": v(-24.31, 29.6) * mm});
            skLineSegment(sketch, "E50.39.8.0", {"start": v(-31.04, 37.78) * mm, "end": v(-32.95, 40.1) * mm});
            skArc(sketch, "E50.3.9.0", {"start": v(-31.96, 21.11) * mm, "mid": v(-33.17, 19.15) * mm, "end": v(-34.26, 17.12) * mm});
            skArc(sketch, "E50.7.9.0", {"start": v(-29.45, 19.46) * mm, "mid": v(-30.57, 17.65) * mm, "end": v(-31.58, 15.78) * mm});
            skLineSegment(sketch, "E50.9.9.0", {"start": v(-43.74, 21.86) * mm, "end": v(-46.43, 23.2) * mm});
            skLineSegment(sketch, "E50.11.9.0", {"start": v(-37.66, 18.82) * mm, "end": v(-40.34, 20.16) * mm});
            skLineSegment(sketch, "E50.14.9.0", {"start": v(-35.13, 23.2) * mm, "end": v(-37.63, 24.86) * mm});
            skArc(sketch, "E50.17.9.0", {"start": v(-35.13, 23.2) * mm, "mid": v(-36.46, 21.05) * mm, "end": v(-37.66, 18.82) * mm});
            skLineSegment(sketch, "E50.21.9.0", {"start": v(-31.58, 15.78) * mm, "end": v(-34.26, 17.12) * mm});
            skArc(sketch, "E50.24.9.0", {"start": v(-40.8, 26.95) * mm, "mid": v(-42.35, 24.45) * mm, "end": v(-43.74, 21.86) * mm});
            skArc(sketch, "E50.28.9.0", {"start": v(-37.63, 24.86) * mm, "mid": v(-39.06, 22.55) * mm, "end": v(-40.34, 20.16) * mm});
            skArc(sketch, "E50.32.9.0", {"start": v(-43.3, 28.6) * mm, "mid": v(-44.95, 25.95) * mm, "end": v(-46.43, 23.2) * mm});
            skLineSegment(sketch, "E50.36.9.0", {"start": v(-29.45, 19.46) * mm, "end": v(-31.96, 21.11) * mm});
            skLineSegment(sketch, "E50.39.9.0", {"start": v(-40.8, 26.95) * mm, "end": v(-43.3, 28.6) * mm});
            skArc(sketch, "E50.3.10.0", {"start": v(-36.76, 10.75) * mm, "mid": v(-37.34, 8.52) * mm, "end": v(-37.78, 6.26) * mm});
            skArc(sketch, "E50.7.10.0", {"start": v(-33.88, 9.91) * mm, "mid": v(-34.41, 7.86) * mm, "end": v(-34.82, 5.77) * mm});
            skLineSegment(sketch, "E50.9.10.0", {"start": v(-48.24, 8) * mm, "end": v(-51.2, 8.48) * mm});
            skLineSegment(sketch, "E50.11.10.0", {"start": v(-41.53, 6.88) * mm, "end": v(-44.5, 7.37) * mm});
            skLineSegment(sketch, "E50.14.10.0", {"start": v(-40.4, 11.82) * mm, "end": v(-43.29, 12.66) * mm});
            skArc(sketch, "E50.17.10.0", {"start": v(-40.4, 11.82) * mm, "mid": v(-41.04, 9.37) * mm, "end": v(-41.53, 6.88) * mm});
            skLineSegment(sketch, "E50.21.10.0", {"start": v(-34.82, 5.77) * mm, "end": v(-37.78, 6.26) * mm});
            skArc(sketch, "E50.24.10.0", {"start": v(-46.93, 13.73) * mm, "mid": v(-47.67, 10.88) * mm, "end": v(-48.24, 8) * mm});
            skArc(sketch, "E50.28.10.0", {"start": v(-43.29, 12.66) * mm, "mid": v(-43.97, 10.04) * mm, "end": v(-44.5, 7.37) * mm});
            skArc(sketch, "E50.32.10.0", {"start": v(-49.81, 14.57) * mm, "mid": v(-50.6, 11.55) * mm, "end": v(-51.2, 8.48) * mm});
            skLineSegment(sketch, "E50.36.10.0", {"start": v(-33.88, 9.91) * mm, "end": v(-36.76, 10.75) * mm});
            skLineSegment(sketch, "E50.39.10.0", {"start": v(-46.93, 13.73) * mm, "end": v(-49.81, 14.57) * mm});
            skArc(sketch, "E50.3.11.0", {"start": v(-38.3, -0.56) * mm, "mid": v(-38.2, -2.86) * mm, "end": v(-37.95, -5.15) * mm});
            skArc(sketch, "E50.7.11.0", {"start": v(-35.3, -0.52) * mm, "mid": v(-35.2, -2.64) * mm, "end": v(-34.98, -4.75) * mm});
            skLineSegment(sketch, "E50.9.11.0", {"start": v(-48.46, -6.58) * mm, "end": v(-51.43, -6.99) * mm});
            skLineSegment(sketch, "E50.11.11.0", {"start": v(-41.72, -5.66) * mm, "end": v(-44.69, -6.07) * mm});
            skLineSegment(sketch, "E50.14.11.0", {"start": v(-42.1, -0.61) * mm, "end": v(-45.1, -0.66) * mm});
            skArc(sketch, "E50.17.11.0", {"start": v(-42.1, -0.61) * mm, "mid": v(-41.98, -3.15) * mm, "end": v(-41.72, -5.66) * mm});
            skLineSegment(sketch, "E50.21.11.0", {"start": v(-34.98, -4.75) * mm, "end": v(-37.95, -5.15) * mm});
            skArc(sketch, "E50.24.11.0", {"start": v(-48.9, -0.71) * mm, "mid": v(-48.76, -3.65) * mm, "end": v(-48.46, -6.58) * mm});
            skArc(sketch, "E50.28.11.0", {"start": v(-45.1, -0.66) * mm, "mid": v(-44.97, -3.37) * mm, "end": v(-44.69, -6.07) * mm});
            skArc(sketch, "E50.32.11.0", {"start": v(-51.9, -0.76) * mm, "mid": v(-51.75, -3.88) * mm, "end": v(-51.43, -6.99) * mm});
            skLineSegment(sketch, "E50.36.11.0", {"start": v(-35.3, -0.52) * mm, "end": v(-38.3, -0.56) * mm});
            skLineSegment(sketch, "E50.39.11.0", {"start": v(-48.9, -0.71) * mm, "end": v(-51.9, -0.76) * mm});
            skArc(sketch, "E50.3.12.0", {"start": v(-36.43, -11.82) * mm, "mid": v(-35.65, -14) * mm, "end": v(-34.75, -16.1) * mm});
            skArc(sketch, "E50.7.12.0", {"start": v(-33.58, -10.9) * mm, "mid": v(-32.86, -12.9) * mm, "end": v(-32.03, -14.85) * mm});
            skLineSegment(sketch, "E50.9.12.0", {"start": v(-44.36, -20.57) * mm, "end": v(-47.08, -21.83) * mm});
            skLineSegment(sketch, "E50.11.12.0", {"start": v(-38.2, -17.7) * mm, "end": v(-40.92, -18.97) * mm});
            skLineSegment(sketch, "E50.14.12.0", {"start": v(-40.04, -13) * mm, "end": v(-42.9, -13.92) * mm});
            skArc(sketch, "E50.17.12.0", {"start": v(-40.04, -13) * mm, "mid": v(-39.2, -15.38) * mm, "end": v(-38.2, -17.7) * mm});
            skLineSegment(sketch, "E50.21.12.0", {"start": v(-32.03, -14.85) * mm, "end": v(-34.75, -16.1) * mm});
            skArc(sketch, "E50.24.12.0", {"start": v(-46.51, -15.1) * mm, "mid": v(-45.52, -17.87) * mm, "end": v(-44.36, -20.57) * mm});
            skArc(sketch, "E50.28.12.0", {"start": v(-42.9, -13.92) * mm, "mid": v(-41.98, -16.48) * mm, "end": v(-40.92, -18.97) * mm});
            skArc(sketch, "E50.32.12.0", {"start": v(-49.37, -16.02) * mm, "mid": v(-48.31, -18.96) * mm, "end": v(-47.08, -21.83) * mm});
            skLineSegment(sketch, "E50.36.12.0", {"start": v(-33.58, -10.9) * mm, "end": v(-36.43, -11.82) * mm});
            skLineSegment(sketch, "E50.39.12.0", {"start": v(-46.51, -15.1) * mm, "end": v(-49.37, -16.02) * mm});
            skArc(sketch, "E50.3.13.0", {"start": v(-31.33, -22.04) * mm, "mid": v(-29.94, -23.88) * mm, "end": v(-28.46, -25.64) * mm});
            skArc(sketch, "E50.7.13.0", {"start": v(-28.87, -20.3) * mm, "mid": v(-27.6, -22) * mm, "end": v(-26.23, -23.63) * mm});
            skLineSegment(sketch, "E50.9.13.0", {"start": v(-36.33, -32.73) * mm, "end": v(-38.56, -34.74) * mm});
            skLineSegment(sketch, "E50.11.13.0", {"start": v(-31.28, -28.18) * mm, "end": v(-33.5, -30.19) * mm});
            skLineSegment(sketch, "E50.14.13.0", {"start": v(-34.43, -24.22) * mm, "end": v(-36.89, -25.95) * mm});
            skArc(sketch, "E50.17.13.0", {"start": v(-34.43, -24.22) * mm, "mid": v(-32.92, -26.25) * mm, "end": v(-31.28, -28.18) * mm});
            skLineSegment(sketch, "E50.21.13.0", {"start": v(-26.23, -23.63) * mm, "end": v(-28.46, -25.64) * mm});
            skArc(sketch, "E50.24.13.0", {"start": v(-40, -28.13) * mm, "mid": v(-38.23, -30.49) * mm, "end": v(-36.33, -32.73) * mm});
            skArc(sketch, "E50.28.13.0", {"start": v(-36.89, -25.95) * mm, "mid": v(-35.26, -28.12) * mm, "end": v(-33.5, -30.19) * mm});
            skArc(sketch, "E50.32.13.0", {"start": v(-42.45, -29.86) * mm, "mid": v(-40.58, -32.36) * mm, "end": v(-38.56, -34.74) * mm});
            skLineSegment(sketch, "E50.36.13.0", {"start": v(-28.87, -20.3) * mm, "end": v(-31.33, -22.04) * mm});
            skLineSegment(sketch, "E50.39.13.0", {"start": v(-40, -28.13) * mm, "end": v(-42.45, -29.86) * mm});
            skArc(sketch, "E50.3.14.0", {"start": v(-23.44, -30.29) * mm, "mid": v(-21.58, -31.64) * mm, "end": v(-19.63, -32.88) * mm});
            skArc(sketch, "E50.7.14.0", {"start": v(-21.6, -27.92) * mm, "mid": v(-19.89, -29.17) * mm, "end": v(-18.1, -30.3) * mm});
            skLineSegment(sketch, "E50.9.14.0", {"start": v(-25.07, -41.99) * mm, "end": v(-26.6, -44.56) * mm});
            skLineSegment(sketch, "E50.11.14.0", {"start": v(-21.58, -36.15) * mm, "end": v(-23.12, -38.72) * mm});
            skLineSegment(sketch, "E50.14.14.0", {"start": v(-25.77, -33.3) * mm, "end": v(-27.6, -35.67) * mm});
            skArc(sketch, "E50.17.14.0", {"start": v(-25.77, -33.3) * mm, "mid": v(-23.72, -34.78) * mm, "end": v(-21.58, -36.15) * mm});
            skLineSegment(sketch, "E50.21.14.0", {"start": v(-18.1, -30.3) * mm, "end": v(-19.63, -32.88) * mm});
            skArc(sketch, "E50.24.14.0", {"start": v(-29.93, -38.67) * mm, "mid": v(-27.55, -40.4) * mm, "end": v(-25.07, -41.99) * mm});
            skArc(sketch, "E50.28.14.0", {"start": v(-27.6, -35.67) * mm, "mid": v(-25.4, -37.26) * mm, "end": v(-23.12, -38.72) * mm});
            skArc(sketch, "E50.32.14.0", {"start": v(-31.76, -41.05) * mm, "mid": v(-29.24, -42.88) * mm, "end": v(-26.6, -44.56) * mm});
            skLineSegment(sketch, "E50.36.14.0", {"start": v(-21.6, -27.92) * mm, "end": v(-23.44, -30.29) * mm});
            skLineSegment(sketch, "E50.39.14.0", {"start": v(-29.93, -38.67) * mm, "end": v(-31.76, -41.05) * mm});
            skArc(sketch, "E50.3.15.0", {"start": v(-13.47, -35.85) * mm, "mid": v(-11.3, -36.6) * mm, "end": v(-9.07, -37.21) * mm});
            skArc(sketch, "E50.7.15.0", {"start": v(-12.42, -33.04) * mm, "mid": v(-10.4, -33.73) * mm, "end": v(-8.36, -34.3) * mm});
            skLineSegment(sketch, "E50.9.15.0", {"start": v(-11.58, -47.5) * mm, "end": v(-12.29, -50.42) * mm});
            skLineSegment(sketch, "E50.11.15.0", {"start": v(-9.97, -40.9) * mm, "end": v(-10.68, -43.82) * mm});
            skLineSegment(sketch, "E50.14.15.0", {"start": v(-14.8, -39.41) * mm, "end": v(-15.86, -42.22) * mm});
            skArc(sketch, "E50.17.15.0", {"start": v(-14.8, -39.41) * mm, "mid": v(-12.41, -40.23) * mm, "end": v(-9.97, -40.9) * mm});
            skLineSegment(sketch, "E50.21.15.0", {"start": v(-8.36, -34.3) * mm, "end": v(-9.07, -37.21) * mm});
            skArc(sketch, "E50.24.15.0", {"start": v(-17.2, -45.78) * mm, "mid": v(-14.41, -46.73) * mm, "end": v(-11.58, -47.5) * mm});
            skArc(sketch, "E50.28.15.0", {"start": v(-15.86, -42.22) * mm, "mid": v(-13.3, -43.1) * mm, "end": v(-10.68, -43.82) * mm});
            skArc(sketch, "E50.32.15.0", {"start": v(-18.25, -48.58) * mm, "mid": v(-15.3, -49.6) * mm, "end": v(-12.29, -50.42) * mm});
            skLineSegment(sketch, "E50.36.15.0", {"start": v(-12.42, -33.04) * mm, "end": v(-13.47, -35.85) * mm});
            skLineSegment(sketch, "E50.39.15.0", {"start": v(-17.2, -45.78) * mm, "end": v(-18.25, -48.58) * mm});
            skArc(sketch, "E50.3.16.0", {"start": v(-2.3, -38.23) * mm, "mid": v(0, -38.3) * mm, "end": v(2.3, -38.23) * mm});
            skArc(sketch, "E50.7.16.0", {"start": v(-2.12, -35.24) * mm, "mid": v(0, -35.3) * mm, "end": v(2.12, -35.24) * mm});
            skLineSegment(sketch, "E50.9.16.0", {"start": v(2.94, -48.81) * mm, "end": v(3.12, -51.8) * mm});
            skLineSegment(sketch, "E50.11.16.0", {"start": v(2.53, -42.02) * mm, "end": v(2.71, -45.02) * mm});
            skLineSegment(sketch, "E50.14.16.0", {"start": v(-2.53, -42.02) * mm, "end": v(-2.71, -45.02) * mm});
            skArc(sketch, "E50.17.16.0", {"start": v(-2.53, -42.02) * mm, "mid": v(0, -42.1) * mm, "end": v(2.53, -42.02) * mm});
            skLineSegment(sketch, "E50.21.16.0", {"start": v(2.12, -35.24) * mm, "end": v(2.3, -38.23) * mm});
            skArc(sketch, "E50.24.16.0", {"start": v(-2.94, -48.81) * mm, "mid": v(0, -48.9) * mm, "end": v(2.94, -48.81) * mm});
            skArc(sketch, "E50.28.16.0", {"start": v(-2.71, -45.02) * mm, "mid": v(0, -45.1) * mm, "end": v(2.71, -45.02) * mm});
            skArc(sketch, "E50.32.16.0", {"start": v(-3.12, -51.8) * mm, "mid": v(0, -51.9) * mm, "end": v(3.12, -51.8) * mm});
            skLineSegment(sketch, "E50.36.16.0", {"start": v(-2.12, -35.24) * mm, "end": v(-2.3, -38.23) * mm});
            skLineSegment(sketch, "E50.39.16.0", {"start": v(-2.94, -48.81) * mm, "end": v(-3.12, -51.8) * mm});
            skArc(sketch, "E50.3.17.0", {"start": v(9.07, -37.21) * mm, "mid": v(11.29, -36.6) * mm, "end": v(13.47, -35.85) * mm});
            skArc(sketch, "E50.7.17.0", {"start": v(8.36, -34.3) * mm, "mid": v(10.4, -33.73) * mm, "end": v(12.41, -33.05) * mm});
            skLineSegment(sketch, "E50.9.17.0", {"start": v(17.2, -45.78) * mm, "end": v(18.25, -48.58) * mm});
            skLineSegment(sketch, "E50.11.17.0", {"start": v(14.8, -39.41) * mm, "end": v(15.86, -42.22) * mm});
            skLineSegment(sketch, "E50.14.17.0", {"start": v(9.97, -40.9) * mm, "end": v(10.68, -43.82) * mm});
            skArc(sketch, "E50.17.17.0", {"start": v(9.97, -40.9) * mm, "mid": v(12.4, -40.23) * mm, "end": v(14.8, -39.41) * mm});
            skLineSegment(sketch, "E50.21.17.0", {"start": v(12.41, -33.05) * mm, "end": v(13.47, -35.85) * mm});
            skArc(sketch, "E50.24.17.0", {"start": v(11.58, -47.5) * mm, "mid": v(14.41, -46.73) * mm, "end": v(17.2, -45.78) * mm});
            skArc(sketch, "E50.28.17.0", {"start": v(10.68, -43.82) * mm, "mid": v(13.3, -43.1) * mm, "end": v(15.86, -42.22) * mm});
            skArc(sketch, "E50.32.17.0", {"start": v(12.29, -50.42) * mm, "mid": v(15.3, -49.6) * mm, "end": v(18.25, -48.58) * mm});
            skLineSegment(sketch, "E50.36.17.0", {"start": v(8.36, -34.3) * mm, "end": v(9.07, -37.21) * mm});
            skLineSegment(sketch, "E50.39.17.0", {"start": v(11.58, -47.5) * mm, "end": v(12.29, -50.42) * mm});
            skArc(sketch, "E50.3.18.0", {"start": v(19.63, -32.89) * mm, "mid": v(21.57, -31.65) * mm, "end": v(23.44, -30.3) * mm});
            skArc(sketch, "E50.7.18.0", {"start": v(18.1, -30.3) * mm, "mid": v(19.88, -29.17) * mm, "end": v(21.6, -27.92) * mm});
            skLineSegment(sketch, "E50.9.18.0", {"start": v(29.93, -38.67) * mm, "end": v(31.76, -41.05) * mm});
            skLineSegment(sketch, "E50.11.18.0", {"start": v(25.76, -33.3) * mm, "end": v(27.6, -35.67) * mm});
            skLineSegment(sketch, "E50.14.18.0", {"start": v(21.58, -36.15) * mm, "end": v(23.12, -38.72) * mm});
            skArc(sketch, "E50.17.18.0", {"start": v(21.58, -36.15) * mm, "mid": v(23.72, -34.79) * mm, "end": v(25.76, -33.3) * mm});
            skLineSegment(sketch, "E50.21.18.0", {"start": v(21.6, -27.92) * mm, "end": v(23.44, -30.3) * mm});
            skArc(sketch, "E50.24.18.0", {"start": v(25.07, -41.99) * mm, "mid": v(27.55, -40.4) * mm, "end": v(29.93, -38.67) * mm});
            skArc(sketch, "E50.28.18.0", {"start": v(23.12, -38.72) * mm, "mid": v(25.4, -37.26) * mm, "end": v(27.6, -35.67) * mm});
            skArc(sketch, "E50.32.18.0", {"start": v(26.6, -44.56) * mm, "mid": v(29.24, -42.88) * mm, "end": v(31.76, -41.05) * mm});
            skLineSegment(sketch, "E50.36.18.0", {"start": v(18.1, -30.3) * mm, "end": v(19.63, -32.89) * mm});
            skLineSegment(sketch, "E50.39.18.0", {"start": v(25.07, -41.99) * mm, "end": v(26.6, -44.56) * mm});
            skArc(sketch, "E50.3.19.0", {"start": v(28.45, -25.64) * mm, "mid": v(29.94, -23.88) * mm, "end": v(31.32, -22.04) * mm});
            skArc(sketch, "E50.7.19.0", {"start": v(26.22, -23.63) * mm, "mid": v(27.6, -22.01) * mm, "end": v(28.87, -20.31) * mm});
            skLineSegment(sketch, "E50.9.19.0", {"start": v(40, -28.13) * mm, "end": v(42.45, -29.86) * mm});
            skLineSegment(sketch, "E50.11.19.0", {"start": v(34.43, -24.22) * mm, "end": v(36.89, -25.95) * mm});
            skLineSegment(sketch, "E50.14.19.0", {"start": v(31.28, -28.18) * mm, "end": v(33.5, -30.19) * mm});
            skArc(sketch, "E50.17.19.0", {"start": v(31.28, -28.18) * mm, "mid": v(32.91, -26.25) * mm, "end": v(34.43, -24.22) * mm});
            skLineSegment(sketch, "E50.21.19.0", {"start": v(28.87, -20.31) * mm, "end": v(31.32, -22.04) * mm});
            skArc(sketch, "E50.24.19.0", {"start": v(36.33, -32.73) * mm, "mid": v(38.23, -30.49) * mm, "end": v(40, -28.13) * mm});
            skArc(sketch, "E50.28.19.0", {"start": v(33.5, -30.19) * mm, "mid": v(35.26, -28.12) * mm, "end": v(36.89, -25.95) * mm});
            skArc(sketch, "E50.32.19.0", {"start": v(38.56, -34.74) * mm, "mid": v(40.58, -32.36) * mm, "end": v(42.45, -29.86) * mm});
            skLineSegment(sketch, "E50.36.19.0", {"start": v(26.22, -23.63) * mm, "end": v(28.45, -25.64) * mm});
            skLineSegment(sketch, "E50.39.19.0", {"start": v(36.33, -32.73) * mm, "end": v(38.56, -34.74) * mm});
            skArc(sketch, "E50.3.20.0", {"start": v(34.75, -16.11) * mm, "mid": v(35.65, -14) * mm, "end": v(36.43, -11.82) * mm});
            skArc(sketch, "E50.7.20.0", {"start": v(32.02, -14.85) * mm, "mid": v(32.86, -12.9) * mm, "end": v(33.58, -10.9) * mm});
            skLineSegment(sketch, "E50.9.20.0", {"start": v(46.51, -15.1) * mm, "end": v(49.37, -16.02) * mm});
            skLineSegment(sketch, "E50.11.20.0", {"start": v(40.04, -13) * mm, "end": v(42.9, -13.92) * mm});
            skLineSegment(sketch, "E50.14.20.0", {"start": v(38.2, -17.71) * mm, "end": v(40.92, -18.97) * mm});
            skArc(sketch, "E50.17.20.0", {"start": v(38.2, -17.71) * mm, "mid": v(39.19, -15.38) * mm, "end": v(40.04, -13) * mm});
            skLineSegment(sketch, "E50.21.20.0", {"start": v(33.58, -10.9) * mm, "end": v(36.43, -11.82) * mm});
            skArc(sketch, "E50.24.20.0", {"start": v(44.36, -20.57) * mm, "mid": v(45.52, -17.87) * mm, "end": v(46.51, -15.1) * mm});
            skArc(sketch, "E50.28.20.0", {"start": v(40.92, -18.97) * mm, "mid": v(41.98, -16.48) * mm, "end": v(42.9, -13.92) * mm});
            skArc(sketch, "E50.32.20.0", {"start": v(47.08, -21.83) * mm, "mid": v(48.31, -18.96) * mm, "end": v(49.37, -16.02) * mm});
            skLineSegment(sketch, "E50.36.20.0", {"start": v(32.02, -14.85) * mm, "end": v(34.75, -16.11) * mm});
            skLineSegment(sketch, "E50.39.20.0", {"start": v(44.36, -20.57) * mm, "end": v(47.08, -21.83) * mm});
            skLineSegment(sketch, "E51", {"start": v(42.1, -0.62) * mm, "end": v(41.72, -5.67) * mm});
            skLineSegment(sketch, "E52", {"start": v(51.9, -0.76) * mm, "end": v(51.43, -6.98) * mm});
            skLineSegment(sketch, "E53", {"start": v(48.9, -0.71) * mm, "end": v(48.46, -6.58) * mm});
            skSolve(sketch);
        }
        {
            var Q0;
            Q0 = qSketchRegion(id + "F10", true);
            extrude(context, id + "F11", {"entities" : qUnion([Q0]), "operationType" : NewBodyOperationType.REMOVE, "oppositeDirection" : true, "depth" : 25 * mm, "offsetDistance" : 25 * mm});
        }
        {
            var Q0;
            Q0=makeQuery(id+"F1.opExtrude","CAP_FACE",FACE,{"disambiguationData":[OSD([sQuery(id+"F0.wireOp",EDGE,"E0"),sQuery(id+"F0.wireOp",EDGE,"E1"),sQuery(id+"F0.wireOp",EDGE,"E6"),sQuery(id+"F0.wireOp",EDGE,"E7"),sQuery(id+"F0.wireOp",EDGE,"E8"),sQuery(id+"F0.wireOp",EDGE,"E9"),sQuery(id+"F0.wireOp",EDGE,"E10"),sQuery(id+"F0.wireOp",EDGE,"E11"),sQuery(id+"F0.wireOp",EDGE,"E12"),sQuery(id+"F0.wireOp",EDGE,"E13.1.0"),sQuery(id+"F0.wireOp",EDGE,"E13.1.1"),sQuery(id+"F0.wireOp",EDGE,"E13.1.2"),sQuery(id+"F0.wireOp",EDGE,"E13.1.3"),sQuery(id+"F0.wireOp",EDGE,"E13.2.0"),sQuery(id+"F0.wireOp",EDGE,"E13.2.1"),sQuery(id+"F0.wireOp",EDGE,"E13.2.2"),sQuery(id+"F0.wireOp",EDGE,"E13.2.3"),sQuery(id+"F0.wireOp",EDGE,"E14.1.3.0"),sQuery(id+"F0.wireOp",EDGE,"E14.2.3.0"),sQuery(id+"F0.wireOp",EDGE,"E14.4.3.0"),sQuery(id+"F0.wireOp",EDGE,"E14.6.3.0"),sQuery(id+"F0.wireOp",EDGE,"E14.1.4.0"),sQuery(id+"F0.wireOp",EDGE,"E14.2.4.0"),sQuery(id+"F0.wireOp",EDGE,"E14.4.4.0"),sQuery(id+"F0.wireOp",EDGE,"E14.6.4.0"),sQuery(id+"F0.wireOp",EDGE,"E14.1.5.0"),sQuery(id+"F0.wireOp",EDGE,"E14.2.5.0"),sQuery(id+"F0.wireOp",EDGE,"E14.4.5.0"),sQuery(id+"F0.wireOp",EDGE,"E14.6.5.0"),sQuery(id+"F0.wireOp",EDGE,"E14.1.6.0"),sQuery(id+"F0.wireOp",EDGE,"E14.2.6.0"),sQuery(id+"F0.wireOp",EDGE,"E14.4.6.0"),sQuery(id+"F0.wireOp",EDGE,"E14.6.6.0"),sQuery(id+"F0.wireOp",EDGE,"E14.1.7.0"),sQuery(id+"F0.wireOp",EDGE,"E14.2.7.0"),sQuery(id+"F0.wireOp",EDGE,"E14.4.7.0"),sQuery(id+"F0.wireOp",EDGE,"E14.6.7.0"),sQuery(id+"F0.wireOp",EDGE,"E14.1.8.0"),sQuery(id+"F0.wireOp",EDGE,"E14.2.8.0"),sQuery(id+"F0.wireOp",EDGE,"E14.4.8.0"),sQuery(id+"F0.wireOp",EDGE,"E14.6.8.0"),sQuery(id+"F0.wireOp",EDGE,"E14.1.9.0"),sQuery(id+"F0.wireOp",EDGE,"E14.2.9.0"),sQuery(id+"F0.wireOp",EDGE,"E14.4.9.0"),sQuery(id+"F0.wireOp",EDGE,"E14.6.9.0"),sQuery(id+"F0.wireOp",EDGE,"E14.1.10.0"),sQuery(id+"F0.wireOp",EDGE,"E14.2.10.0"),sQuery(id+"F0.wireOp",EDGE,"E14.4.10.0"),sQuery(id+"F0.wireOp",EDGE,"E14.6.10.0"),sQuery(id+"F0.wireOp",EDGE,"E14.1.11.0"),sQuery(id+"F0.wireOp",EDGE,"E14.2.11.0"),sQuery(id+"F0.wireOp",EDGE,"E14.4.11.0"),sQuery(id+"F0.wireOp",EDGE,"E14.6.11.0"),sQuery(id+"F0.wireOp",EDGE,"E14.1.12.0"),sQuery(id+"F0.wireOp",EDGE,"E14.2.12.0"),sQuery(id+"F0.wireOp",EDGE,"E14.4.12.0"),sQuery(id+"F0.wireOp",EDGE,"E14.6.12.0"),sQuery(id+"F0.wireOp",EDGE,"E14.1.13.0"),sQuery(id+"F0.wireOp",EDGE,"E14.2.13.0"),sQuery(id+"F0.wireOp",EDGE,"E14.4.13.0"),sQuery(id+"F0.wireOp",EDGE,"E14.6.13.0"),sQuery(id+"F0.wireOp",EDGE,"E14.1.14.0"),sQuery(id+"F0.wireOp",EDGE,"E14.2.14.0"),sQuery(id+"F0.wireOp",EDGE,"E14.4.14.0"),sQuery(id+"F0.wireOp",EDGE,"E14.6.14.0"),sQuery(id+"F0.wireOp",EDGE,"E14.1.15.0"),sQuery(id+"F0.wireOp",EDGE,"E14.2.15.0"),sQuery(id+"F0.wireOp",EDGE,"E14.4.15.0"),sQuery(id+"F0.wireOp",EDGE,"E14.6.15.0"),sQuery(id+"F0.wireOp",EDGE,"E14.1.16.0"),sQuery(id+"F0.wireOp",EDGE,"E14.2.16.0"),sQuery(id+"F0.wireOp",EDGE,"E14.4.16.0"),sQuery(id+"F0.wireOp",EDGE,"E14.6.16.0"),sQuery(id+"F0.wireOp",EDGE,"E14.1.17.0"),sQuery(id+"F0.wireOp",EDGE,"E14.2.17.0"),sQuery(id+"F0.wireOp",EDGE,"E14.4.17.0"),sQuery(id+"F0.wireOp",EDGE,"E14.6.17.0"),sQuery(id+"F0.wireOp",EDGE,"E14.1.18.0"),sQuery(id+"F0.wireOp",EDGE,"E14.2.18.0"),sQuery(id+"F0.wireOp",EDGE,"E14.4.18.0"),sQuery(id+"F0.wireOp",EDGE,"E14.6.18.0"),sQuery(id+"F0.wireOp",EDGE,"E14.1.19.0"),sQuery(id+"F0.wireOp",EDGE,"E14.2.19.0"),sQuery(id+"F0.wireOp",EDGE,"E14.4.19.0"),sQuery(id+"F0.wireOp",EDGE,"E14.6.19.0"),sQuery(id+"F0.wireOp",EDGE,"E14.1.20.0"),sQuery(id+"F0.wireOp",EDGE,"E14.2.20.0"),sQuery(id+"F0.wireOp",EDGE,"E14.4.20.0"),sQuery(id+"F0.wireOp",EDGE,"E14.6.20.0"),sQuery(id+"F0.wireOp",EDGE,"E16"),sQuery(id+"F0.wireOp",EDGE,"E17"),sQuery(id+"F0.wireOp",EDGE,"E18"),sQuery(id+"F0.wireOp",EDGE,"E19"),sQuery(id+"F0.wireOp",EDGE,"E20"),sQuery(id+"F0.wireOp",EDGE,"E21.1.0"),sQuery(id+"F0.wireOp",EDGE,"E21.1.1"),sQuery(id+"F0.wireOp",EDGE,"E21.1.2"),sQuery(id+"F0.wireOp",EDGE,"E21.1.3"),sQuery(id+"F0.wireOp",EDGE,"E21.1.4"),sQuery(id+"F0.wireOp",EDGE,"E21.1.5"),sQuery(id+"F0.wireOp",EDGE,"E21.1.6"),sQuery(id+"F0.wireOp",EDGE,"E21.1.7"),sQuery(id+"F0.wireOp",EDGE,"E21.2.0"),sQuery(id+"F0.wireOp",EDGE,"E21.2.1"),sQuery(id+"F0.wireOp",EDGE,"E21.2.2"),sQuery(id+"F0.wireOp",EDGE,"E21.2.3"),sQuery(id+"F0.wireOp",EDGE,"E21.2.4"),sQuery(id+"F0.wireOp",EDGE,"E21.2.5"),sQuery(id+"F0.wireOp",EDGE,"E21.2.6"),sQuery(id+"F0.wireOp",EDGE,"E21.2.7")])],"isStart":false});
            var sketch = newSketch(context, id + "F12", { "sketchPlane" : qUnion([Q0])});
            skCircle(sketch, "E54", {"center": v(-47.94, -15.56) * mm, "radius": 1.5 * mm});
            skCircle(sketch, "E55", {"center": v(-45.72, -21.2) * mm, "radius": 1.5 * mm});
            skCircle(sketch, "E56", {"center": v(-39.55, -18.34) * mm, "radius": 1.5 * mm});
            skCircle(sketch, "E57", {"center": v(-41.47, -13.46) * mm, "radius": 1.5 * mm});
            skCircle(sketch, "E58", {"center": v(-35, -11.36) * mm, "radius": 1.5 * mm});
            skCircle(sketch, "E59", {"center": v(-33.39, -15.48) * mm, "radius": 1.5 * mm});
            skCircle(sketch, "E60.1.0", {"center": v(-37.44, -33.74) * mm, "radius": 1.5 * mm});
            skCircle(sketch, "E60.1.1", {"center": v(-41.22, -29) * mm, "radius": 1.5 * mm});
            skCircle(sketch, "E60.1.2", {"center": v(-32.4, -29.18) * mm, "radius": 1.5 * mm});
            skCircle(sketch, "E60.1.3", {"center": v(-35.66, -25.08) * mm, "radius": 1.5 * mm});
            skCircle(sketch, "E60.1.4", {"center": v(-30.1, -21.17) * mm, "radius": 1.5 * mm});
            skCircle(sketch, "E60.1.5", {"center": v(-27.34, -24.63) * mm, "radius": 1.5 * mm});
            skCircle(sketch, "E60.2.0", {"center": v(-25.83, -43.28) * mm, "radius": 1.5 * mm});
            skCircle(sketch, "E60.2.1", {"center": v(-30.85, -39.86) * mm, "radius": 1.5 * mm});
            skCircle(sketch, "E60.2.2", {"center": v(-22.35, -37.44) * mm, "radius": 1.5 * mm});
            skCircle(sketch, "E60.2.3", {"center": v(-26.68, -34.48) * mm, "radius": 1.5 * mm});
            skCircle(sketch, "E60.2.4", {"center": v(-22.52, -29.1) * mm, "radius": 1.5 * mm});
            skCircle(sketch, "E60.2.5", {"center": v(-18.87, -31.6) * mm, "radius": 1.5 * mm});
            skPoint(sketch, "E60.center", {"position": v(0, 0) * mm});
            skCircle(sketch, "E61.1.3.0", {"center": v(-11.93, -48.97) * mm, "radius": 1.5 * mm});
            skCircle(sketch, "E61.2.3.0", {"center": v(-17.73, -47.18) * mm, "radius": 1.5 * mm});
            skCircle(sketch, "E61.4.3.0", {"center": v(-10.32, -42.36) * mm, "radius": 1.5 * mm});
            skCircle(sketch, "E61.6.3.0", {"center": v(-15.33, -40.81) * mm, "radius": 1.5 * mm});
            skCircle(sketch, "E61.8.3.0", {"center": v(-12.94, -34.45) * mm, "radius": 1.5 * mm});
            skCircle(sketch, "E61.10.3.0", {"center": v(-8.71, -35.75) * mm, "radius": 1.5 * mm});
            skCircle(sketch, "E61.1.4.0", {"center": v(3.03, -50.3) * mm, "radius": 1.5 * mm});
            skCircle(sketch, "E61.2.4.0", {"center": v(-3.03, -50.3) * mm, "radius": 1.5 * mm});
            skCircle(sketch, "E61.4.4.0", {"center": v(2.62, -43.52) * mm, "radius": 1.5 * mm});
            skCircle(sketch, "E61.6.4.0", {"center": v(-2.62, -43.52) * mm, "radius": 1.5 * mm});
            skCircle(sketch, "E61.8.4.0", {"center": v(-2.21, -36.73) * mm, "radius": 1.5 * mm});
            skCircle(sketch, "E61.10.4.0", {"center": v(2.21, -36.73) * mm, "radius": 1.5 * mm});
            skCircle(sketch, "E61.1.5.0", {"center": v(17.73, -47.18) * mm, "radius": 1.5 * mm});
            skCircle(sketch, "E61.2.5.0", {"center": v(11.93, -48.97) * mm, "radius": 1.5 * mm});
            skCircle(sketch, "E61.4.5.0", {"center": v(15.33, -40.81) * mm, "radius": 1.5 * mm});
            skCircle(sketch, "E61.6.5.0", {"center": v(10.32, -42.36) * mm, "radius": 1.5 * mm});
            skCircle(sketch, "E61.8.5.0", {"center": v(8.71, -35.75) * mm, "radius": 1.5 * mm});
            skCircle(sketch, "E61.10.5.0", {"center": v(12.94, -34.45) * mm, "radius": 1.5 * mm});
            skCircle(sketch, "E61.1.6.0", {"center": v(30.85, -39.86) * mm, "radius": 1.5 * mm});
            skCircle(sketch, "E61.2.6.0", {"center": v(25.83, -43.27) * mm, "radius": 1.5 * mm});
            skCircle(sketch, "E61.4.6.0", {"center": v(26.68, -34.48) * mm, "radius": 1.5 * mm});
            skCircle(sketch, "E61.6.6.0", {"center": v(22.35, -37.44) * mm, "radius": 1.5 * mm});
            skCircle(sketch, "E61.8.6.0", {"center": v(18.86, -31.6) * mm, "radius": 1.5 * mm});
            skCircle(sketch, "E61.10.6.0", {"center": v(22.52, -29.1) * mm, "radius": 1.5 * mm});
            skCircle(sketch, "E61.1.7.0", {"center": v(41.22, -29) * mm, "radius": 1.5 * mm});
            skCircle(sketch, "E61.2.7.0", {"center": v(37.44, -33.74) * mm, "radius": 1.5 * mm});
            skCircle(sketch, "E61.4.7.0", {"center": v(35.66, -25.09) * mm, "radius": 1.5 * mm});
            skCircle(sketch, "E61.6.7.0", {"center": v(32.4, -29.19) * mm, "radius": 1.5 * mm});
            skCircle(sketch, "E61.8.7.0", {"center": v(27.34, -24.63) * mm, "radius": 1.5 * mm});
            skCircle(sketch, "E61.10.7.0", {"center": v(30.1, -21.17) * mm, "radius": 1.5 * mm});
            skCircle(sketch, "E61.1.8.0", {"center": v(47.94, -15.56) * mm, "radius": 1.5 * mm});
            skCircle(sketch, "E61.2.8.0", {"center": v(45.72, -21.2) * mm, "radius": 1.5 * mm});
            skCircle(sketch, "E61.4.8.0", {"center": v(41.47, -13.46) * mm, "radius": 1.5 * mm});
            skCircle(sketch, "E61.6.8.0", {"center": v(39.55, -18.34) * mm, "radius": 1.5 * mm});
            skCircle(sketch, "E61.8.8.0", {"center": v(33.39, -15.48) * mm, "radius": 1.5 * mm});
            skCircle(sketch, "E61.10.8.0", {"center": v(35, -11.36) * mm, "radius": 1.5 * mm});
            skCircle(sketch, "E61.1.9.0", {"center": v(50.4, -0.74) * mm, "radius": 1.5 * mm});
            skCircle(sketch, "E61.2.9.0", {"center": v(49.94, -6.78) * mm, "radius": 1.5 * mm});
            skCircle(sketch, "E61.4.9.0", {"center": v(43.6, -0.64) * mm, "radius": 1.5 * mm});
            skCircle(sketch, "E61.6.9.0", {"center": v(43.2, -5.87) * mm, "radius": 1.5 * mm});
            skCircle(sketch, "E61.8.9.0", {"center": v(36.47, -4.95) * mm, "radius": 1.5 * mm});
            skCircle(sketch, "E61.10.9.0", {"center": v(36.8, -0.54) * mm, "radius": 1.5 * mm});
            skCircle(sketch, "E61.1.10.0", {"center": v(48.37, 14.15) * mm, "radius": 1.5 * mm});
            skCircle(sketch, "E61.2.10.0", {"center": v(49.72, 8.24) * mm, "radius": 1.5 * mm});
            skCircle(sketch, "E61.4.10.0", {"center": v(41.85, 12.24) * mm, "radius": 1.5 * mm});
            skCircle(sketch, "E61.6.10.0", {"center": v(43.01, 7.13) * mm, "radius": 1.5 * mm});
            skCircle(sketch, "E61.8.10.0", {"center": v(36.3, 6.02) * mm, "radius": 1.5 * mm});
            skCircle(sketch, "E61.10.10.0", {"center": v(35.32, 10.33) * mm, "radius": 1.5 * mm});
            skCircle(sketch, "E61.1.11.0", {"center": v(42.05, 27.78) * mm, "radius": 1.5 * mm});
            skCircle(sketch, "E61.2.11.0", {"center": v(45.08, 22.53) * mm, "radius": 1.5 * mm});
            skCircle(sketch, "E61.4.11.0", {"center": v(36.38, 24.03) * mm, "radius": 1.5 * mm});
            skCircle(sketch, "E61.6.11.0", {"center": v(39, 19.49) * mm, "radius": 1.5 * mm});
            skCircle(sketch, "E61.8.11.0", {"center": v(32.92, 16.45) * mm, "radius": 1.5 * mm});
            skCircle(sketch, "E61.10.11.0", {"center": v(30.7, 20.28) * mm, "radius": 1.5 * mm});
            skCircle(sketch, "E61.1.12.0", {"center": v(32, 38.94) * mm, "radius": 1.5 * mm});
            skCircle(sketch, "E61.2.12.0", {"center": v(36.44, 34.82) * mm, "radius": 1.5 * mm});
            skCircle(sketch, "E61.4.12.0", {"center": v(27.68, 33.69) * mm, "radius": 1.5 * mm});
            skCircle(sketch, "E61.6.12.0", {"center": v(31.52, 30.12) * mm, "radius": 1.5 * mm});
            skCircle(sketch, "E61.8.12.0", {"center": v(26.6, 25.42) * mm, "radius": 1.5 * mm});
            skCircle(sketch, "E61.10.12.0", {"center": v(23.36, 28.43) * mm, "radius": 1.5 * mm});
            skCircle(sketch, "E61.1.13.0", {"center": v(19.1, 46.64) * mm, "radius": 1.5 * mm});
            skCircle(sketch, "E61.2.13.0", {"center": v(24.56, 44.01) * mm, "radius": 1.5 * mm});
            skCircle(sketch, "E61.4.13.0", {"center": v(16.52, 40.35) * mm, "radius": 1.5 * mm});
            skCircle(sketch, "E61.6.13.0", {"center": v(21.25, 38.07) * mm, "radius": 1.5 * mm});
            skCircle(sketch, "E61.8.13.0", {"center": v(17.93, 32.14) * mm, "radius": 1.5 * mm});
            skCircle(sketch, "E61.10.13.0", {"center": v(13.95, 34.06) * mm, "radius": 1.5 * mm});
            skCircle(sketch, "E61.1.14.0", {"center": v(4.5, 50.2) * mm, "radius": 1.5 * mm});
            skCircle(sketch, "E61.2.14.0", {"center": v(10.5, 49.3) * mm, "radius": 1.5 * mm});
            skCircle(sketch, "E61.4.14.0", {"center": v(3.9, 43.43) * mm, "radius": 1.5 * mm});
            skCircle(sketch, "E61.6.14.0", {"center": v(9.08, 42.64) * mm, "radius": 1.5 * mm});
            skCircle(sketch, "E61.8.14.0", {"center": v(7.66, 36) * mm, "radius": 1.5 * mm});
            skCircle(sketch, "E61.10.14.0", {"center": v(3.29, 36.65) * mm, "radius": 1.5 * mm});
            skCircle(sketch, "E61.1.15.0", {"center": v(-10.5, 49.3) * mm, "radius": 1.5 * mm});
            skCircle(sketch, "E61.2.15.0", {"center": v(-4.5, 50.2) * mm, "radius": 1.5 * mm});
            skCircle(sketch, "E61.4.15.0", {"center": v(-9.08, 42.64) * mm, "radius": 1.5 * mm});
            skCircle(sketch, "E61.6.15.0", {"center": v(-3.9, 43.43) * mm, "radius": 1.5 * mm});
            skCircle(sketch, "E61.8.15.0", {"center": v(-3.29, 36.65) * mm, "radius": 1.5 * mm});
            skCircle(sketch, "E61.10.15.0", {"center": v(-7.66, 36) * mm, "radius": 1.5 * mm});
            skCircle(sketch, "E61.1.16.0", {"center": v(-24.56, 44.01) * mm, "radius": 1.5 * mm});
            skCircle(sketch, "E61.2.16.0", {"center": v(-19.1, 46.64) * mm, "radius": 1.5 * mm});
            skCircle(sketch, "E61.4.16.0", {"center": v(-21.24, 38.07) * mm, "radius": 1.5 * mm});
            skCircle(sketch, "E61.6.16.0", {"center": v(-16.52, 40.35) * mm, "radius": 1.5 * mm});
            skCircle(sketch, "E61.8.16.0", {"center": v(-13.94, 34.06) * mm, "radius": 1.5 * mm});
            skCircle(sketch, "E61.10.16.0", {"center": v(-17.93, 32.14) * mm, "radius": 1.5 * mm});
            skCircle(sketch, "E61.1.17.0", {"center": v(-36.44, 34.82) * mm, "radius": 1.5 * mm});
            skCircle(sketch, "E61.2.17.0", {"center": v(-32, 38.94) * mm, "radius": 1.5 * mm});
            skCircle(sketch, "E61.4.17.0", {"center": v(-31.52, 30.12) * mm, "radius": 1.5 * mm});
            skCircle(sketch, "E61.6.17.0", {"center": v(-27.68, 33.69) * mm, "radius": 1.5 * mm});
            skCircle(sketch, "E61.8.17.0", {"center": v(-23.36, 28.43) * mm, "radius": 1.5 * mm});
            skCircle(sketch, "E61.10.17.0", {"center": v(-26.6, 25.42) * mm, "radius": 1.5 * mm});
            skCircle(sketch, "E61.1.18.0", {"center": v(-45.08, 22.53) * mm, "radius": 1.5 * mm});
            skCircle(sketch, "E61.2.18.0", {"center": v(-42.05, 27.78) * mm, "radius": 1.5 * mm});
            skCircle(sketch, "E61.4.18.0", {"center": v(-39, 19.5) * mm, "radius": 1.5 * mm});
            skCircle(sketch, "E61.6.18.0", {"center": v(-36.38, 24.03) * mm, "radius": 1.5 * mm});
            skCircle(sketch, "E61.8.18.0", {"center": v(-30.7, 20.28) * mm, "radius": 1.5 * mm});
            skCircle(sketch, "E61.10.18.0", {"center": v(-32.92, 16.45) * mm, "radius": 1.5 * mm});
            skCircle(sketch, "E61.1.19.0", {"center": v(-49.72, 8.24) * mm, "radius": 1.5 * mm});
            skCircle(sketch, "E61.2.19.0", {"center": v(-48.37, 14.15) * mm, "radius": 1.5 * mm});
            skCircle(sketch, "E61.4.19.0", {"center": v(-43.01, 7.13) * mm, "radius": 1.5 * mm});
            skCircle(sketch, "E61.6.19.0", {"center": v(-41.85, 12.24) * mm, "radius": 1.5 * mm});
            skCircle(sketch, "E61.8.19.0", {"center": v(-35.32, 10.33) * mm, "radius": 1.5 * mm});
            skCircle(sketch, "E61.10.19.0", {"center": v(-36.3, 6.02) * mm, "radius": 1.5 * mm});
            skCircle(sketch, "E61.1.20.0", {"center": v(-49.94, -6.78) * mm, "radius": 1.5 * mm});
            skCircle(sketch, "E61.2.20.0", {"center": v(-50.4, -0.74) * mm, "radius": 1.5 * mm});
            skCircle(sketch, "E61.4.20.0", {"center": v(-43.2, -5.87) * mm, "radius": 1.5 * mm});
            skCircle(sketch, "E61.6.20.0", {"center": v(-43.6, -0.64) * mm, "radius": 1.5 * mm});
            skCircle(sketch, "E61.8.20.0", {"center": v(-36.8, -0.54) * mm, "radius": 1.5 * mm});
            skCircle(sketch, "E61.10.20.0", {"center": v(-36.47, -4.95) * mm, "radius": 1.5 * mm});
            skSolve(sketch);
        }
        {
            var Q0;
            Q0 = qSketchRegion(id + "F12", true);
            extrude(context, id + "F13", {"entities" : qUnion([Q0]), "operationType" : NewBodyOperationType.REMOVE, "oppositeDirection" : true, "depth" : 25 * mm, "offsetDistance" : 25 * mm});
        }
    });
